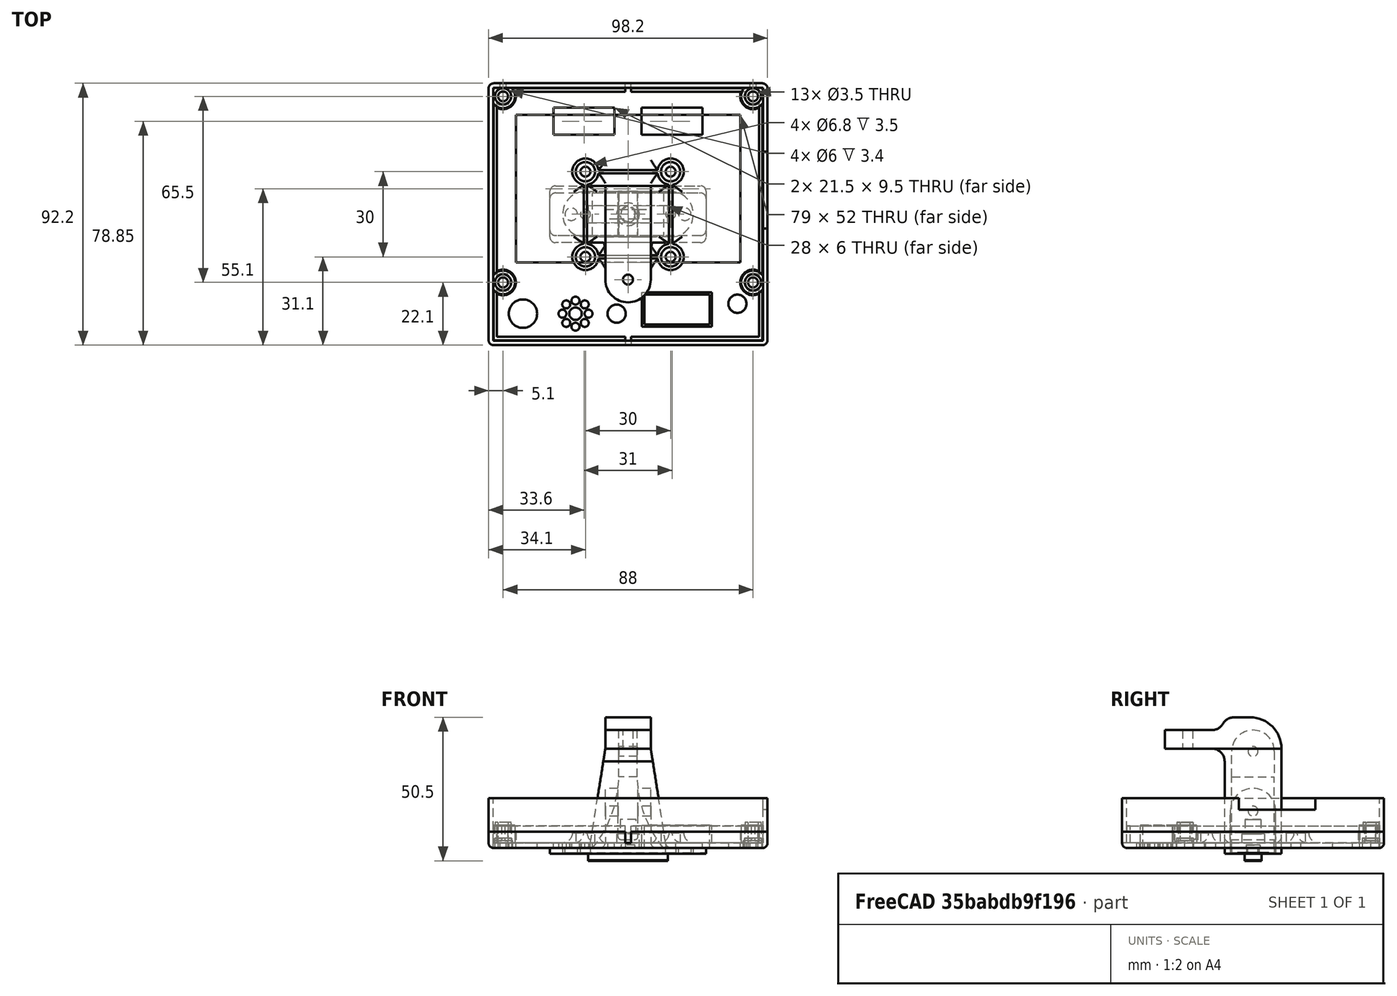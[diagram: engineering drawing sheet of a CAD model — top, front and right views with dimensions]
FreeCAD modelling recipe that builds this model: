
FCSTD DOCUMENT  (FreeCAD 0.17R13522 (Git))
Label: RRDFGSC_case
License: All rights reserved
LicenseURL: http://en.wikipedia.org/wiki/All_rights_reserved
objects: Sketcher::SketchObject×39, PartDesign::Pad×24, PartDesign::Fillet×10, PartDesign::Body×7, App::Part×7, PartDesign::Pocket×5, Spreadsheet::Sheet×2, PartDesign::AdditiveLoft×2
note: 118 computed .brp shape members not serialized (recipe doc carries the construction recipe); baked Part::Feature solids carry a one-line shape summary decoded from their .brp

FEATURE [Sketcher::SketchObject] Sketch  label="frontpanel"
  MapMode = 5
  expr: Constraints[124] = Dimensions.VMHeight
  expr: Constraints.Width = Dimensions.PCBWidth + Dimensions.PCBGap * 2 + Dimensions.WallThickness * 2
  expr: Constraints[95] = Dimensions.LCDGap
  expr: Constraints[123] = Dimensions.VMWidth
  expr: Constraints[11] = Dimensions.PCBHeight + Dimensions.PCBGap * 2 + Dimensions.WallThickness * 2
  expr: Constraints[21] = Dimensions.LCDWidth + Dimensions.LCDGap * 2
  expr: Constraints[93] = Dimensions.LCDHeight
  expr: Constraints[114] = Screws.M3HeadRadius
  expr: Constraints[112] = Dimensions.PCBHeight / 2 - Dimensions.HoleDistanceTop
  expr: Constraints[113] = Dimensions.HoleDistanceV
  expr: Constraints[94] = Dimensions.LCDGap
  expr: Constraints[108] = Dimensions.HoleDistanceH
  expr: Constraints[22] = Dimensions.LCDHeight + Dimensions.LCDGap * 2
  expr: Constraints[33] = Dimensions.PCBWidth
  expr: Constraints[96] = Dimensions.LCDWidth
  expr: Constraints[34] = Dimensions.PCBHeight
  sketch-geometry (48):
    g0: LineSegment StartX=-49.1 StartY=46.1 StartZ=0 EndX=49.1 EndY=46.1 EndZ=0
    g1: LineSegment StartX=49.1 StartY=46.1 StartZ=0 EndX=49.1 EndY=-46.1 EndZ=0
    g2: LineSegment StartX=49.1 StartY=-46.1 StartZ=0 EndX=-49.1 EndY=-46.1 EndZ=0
    g3: LineSegment StartX=-49.1 StartY=-46.1 StartZ=0 EndX=-49.1 EndY=46.1 EndZ=0
    g4: LineSegment StartX=-39.5 StartY=35 StartZ=0 EndX=39.5 EndY=35 EndZ=0
    g5: LineSegment StartX=39.5 StartY=35 StartZ=0 EndX=39.5 EndY=-17 EndZ=0
    g6: LineSegment StartX=39.5 StartY=-17 StartZ=0 EndX=-39.5 EndY=-17 EndZ=0
    g7: LineSegment StartX=-39.5 StartY=-17 StartZ=0 EndX=-39.5 EndY=35 EndZ=0
    g8: Circle CenterX=-37 CenterY=-35 CenterZ=0 NormalX=0 NormalY=0 NormalZ=1 AngleXU=0 Radius=5
    g9: LineSegment [constr] StartX=-46.5 StartY=43.5 StartZ=0 EndX=46.5 EndY=43.5 EndZ=0
    g10: LineSegment [constr] StartX=46.5 StartY=43.5 StartZ=0 EndX=46.5 EndY=-43.5 EndZ=0
    g11: LineSegment [constr] StartX=46.5 StartY=-43.5 StartZ=0 EndX=-46.5 EndY=-43.5 EndZ=0
    g12: LineSegment [constr] StartX=-46.5 StartY=-43.5 StartZ=0 EndX=-46.5 EndY=43.5 EndZ=0
    g13: Circle [constr] CenterX=-18.5 CenterY=-35 CenterZ=0 NormalX=0 NormalY=0 NormalZ=1 AngleXU=0 Radius=6
    g14: LineSegment [constr] StartX=-49.1 StartY=-35 StartZ=0 EndX=49.1 EndY=-35 EndZ=0
    g15: Circle CenterX=-4 CenterY=-35 CenterZ=0 NormalX=0 NormalY=0 NormalZ=1 AngleXU=0 Radius=3.2
    g16: Circle CenterX=-23.1 CenterY=-35 CenterZ=0 NormalX=0 NormalY=0 NormalZ=1 AngleXU=0 Radius=1.4
    g17: LineSegment [constr] StartX=-18.5 StartY=-29 StartZ=0 EndX=-18.5 EndY=-41 EndZ=0
    g18: Circle CenterX=-18.5 CenterY=-30.4 CenterZ=0 NormalX=0 NormalY=0 NormalZ=1 AngleXU=0 Radius=1.4
    g19: Circle CenterX=-13.9 CenterY=-35 CenterZ=0 NormalX=0 NormalY=0 NormalZ=1 AngleXU=0 Radius=1.4
    g20: Circle CenterX=-18.5 CenterY=-39.6 CenterZ=0 NormalX=0 NormalY=0 NormalZ=1 AngleXU=0 Radius=1.4
    g21: Circle CenterX=-18.5 CenterY=-35 CenterZ=0 NormalX=0 NormalY=0 NormalZ=1 AngleXU=0 Radius=2.2
    g22: LineSegment [constr] StartX=-22.7426 StartY=-30.7574 StartZ=0 EndX=-14.2574 EndY=-39.2426 EndZ=0
    g23: LineSegment [constr] StartX=-22.7426 StartY=-39.2426 StartZ=0 EndX=-14.2574 EndY=-30.7574 EndZ=0
    g24: Circle [constr] CenterX=-18.5 CenterY=-35 CenterZ=0 NormalX=0 NormalY=0 NormalZ=1 AngleXU=0 Radius=4.6
    g25: Circle CenterX=-21.7527 CenterY=-31.7473 CenterZ=0 NormalX=0 NormalY=0 NormalZ=1 AngleXU=0 Radius=1.4
    g26: Circle CenterX=-15.2473 CenterY=-31.7473 CenterZ=0 NormalX=0 NormalY=0 NormalZ=1 AngleXU=0 Radius=1.4
    g27: Circle CenterX=-15.2473 CenterY=-38.2527 CenterZ=0 NormalX=0 NormalY=0 NormalZ=1 AngleXU=0 Radius=1.4
    g28: Circle CenterX=-21.7527 CenterY=-38.2527 CenterZ=0 NormalX=0 NormalY=0 NormalZ=1 AngleXU=0 Radius=1.4
    g29: LineSegment [constr] StartX=-39 StartY=34.5 StartZ=0 EndX=39 EndY=34.5 EndZ=0
    g30: LineSegment [constr] StartX=39 StartY=34.5 StartZ=0 EndX=39 EndY=-16.5 EndZ=0
    g31: LineSegment [constr] StartX=39 StartY=-16.5 StartZ=0 EndX=-39 EndY=-16.5 EndZ=0
    g32: LineSegment [constr] StartX=-39 StartY=-16.5 StartZ=0 EndX=-39 EndY=34.5 EndZ=0
    g33: Circle CenterX=38.5 CenterY=-31.5 CenterZ=0 NormalX=0 NormalY=0 NormalZ=1 AngleXU=0 Radius=3.2
    g34: Circle CenterX=-44 CenterY=41.5 CenterZ=0 NormalX=0 NormalY=0 NormalZ=1 AngleXU=0 Radius=3
    g35: Circle CenterX=44 CenterY=41.5 CenterZ=0 NormalX=0 NormalY=0 NormalZ=1 AngleXU=0 Radius=3
    g36: LineSegment [constr] StartX=-44 StartY=41.5 StartZ=0 EndX=44 EndY=41.5 EndZ=0
    g37: Circle CenterX=-44 CenterY=-24 CenterZ=0 NormalX=0 NormalY=0 NormalZ=1 AngleXU=0 Radius=3
    g38: Circle CenterX=44 CenterY=-24 CenterZ=0 NormalX=0 NormalY=0 NormalZ=1 AngleXU=0 Radius=3
    g39: LineSegment [constr] StartX=-44 StartY=-24 StartZ=0 EndX=44 EndY=-24 EndZ=0
    g40: LineSegment StartX=5.75 StartY=-28.3 StartZ=0 EndX=28.75 EndY=-28.3 EndZ=0
    g41: LineSegment StartX=28.75 StartY=-28.3 StartZ=0 EndX=28.75 EndY=-38.8 EndZ=0
    g42: LineSegment StartX=28.75 StartY=-38.8 StartZ=0 EndX=5.75 EndY=-38.8 EndZ=0
    g43: LineSegment StartX=5.75 StartY=-38.8 StartZ=0 EndX=5.75 EndY=-28.3 EndZ=0
    g44: LineSegment [constr] StartX=17.25 StartY=-28.3 StartZ=0 EndX=17.25 EndY=-38.8 EndZ=0
    g45: GeomPoint X=17.25 Y=-33.25 Z=0
    g46: LineSegment [constr] StartX=28.75 StartY=-28.3 StartZ=0 EndX=38.5 EndY=-28.3 EndZ=0
    g47: LineSegment [constr] StartX=38.5 StartY=-31.5 StartZ=0 EndX=38.5 EndY=-28.3 EndZ=0
  constraints (140):
    c: Coincident(g0,g1)
    c: Coincident(g1,g2)
    c: Coincident(g2,g3)
    c: Coincident(g3,g0)
    c: Horizontal(g0)
    c: Horizontal(g2)
    c: Vertical(g1)
    c: Vertical(g3)
    c: Symmetric(g0,g0,g-2)
    c: Symmetric(g0,g2,g-1)
    c: DistanceX(g0,g0) = 98.2  'Width'
    c: DistanceY(g3,g3) = 92.2
    c: Coincident(g4,g5)
    c: Coincident(g5,g6)
    c: Coincident(g6,g7)
    c: Coincident(g7,g4)
    c: Horizontal(g4)
    c: Horizontal(g6)
    c: Vertical(g5)
    c: Vertical(g7)
    c: Symmetric(g4,g4,g-2)
    c: DistanceX(g4,g4) = 79
    c: DistanceY(g7,g7) = 52
    c: Coincident(g9,g10)
    c: Coincident(g10,g11)
    c: Coincident(g11,g12)
    c: Coincident(g12,g9)
    c: Horizontal(g9)
    c: Horizontal(g11)
    c: Vertical(g10)
    c: Vertical(g12)
    c: Symmetric(g9,g9,g-2)
    c: Symmetric(g9,g11,g-1)
    c: DistanceX(g9,g9) = 93
    c: DistanceY(g12,g12) = 87
    c: DistanceX(g11,g8) = 9.5
    c: DistanceY(g11,g8) = 8.5
    c: Radius(g8) = 5
    c: PointOnObject(g14,g3)
    c: PointOnObject(g14,g1)
    c: Horizontal(g14)
    c: PointOnObject(g8,g14)
    c: PointOnObject(g13,g14)
    c: DistanceX(g11,g13) = 28
    c: Radius(g13) = 6
    c: PointOnObject(g15,g14)
    c: Radius(g15) = 3.2
    c: PointOnObject(g16,g14)
    c: Tangent(g13,g16)
    c: Radius(g16) = 1.4
    c: PointOnObject(g17,g13)
    c: PointOnObject(g17,g13)
    c: Vertical(g17)
    c: PointOnObject(g13,g17)
    c: PointOnObject(g18,g17)
    c: Tangent(g18,g13)
    c: Equal(g16,g18)
    c: PointOnObject(g19,g14)
    c: Tangent(g19,g13)
    c: Equal(g16,g19)
    c: PointOnObject(g20,g17)
    c: Tangent(g20,g13)
    c: Equal(g16,g20)
    c: Coincident(g21,g13)
    c: PointOnObject(g22,g13)
    c: PointOnObject(g22,g13)
    c: Symmetric(g18,g16,g22)
    c: PointOnObject(g23,g13)
    c: PointOnObject(g23,g13)
    c: Symmetric(g19,g18,g23)
    c: Coincident(g24,g13)
    c: PointOnObject(g19,g24)
    c: PointOnObject(g25,g22)
    c: PointOnObject(g26,g23)
    c: PointOnObject(g27,g22)
    c: PointOnObject(g28,g24)
    c: PointOnObject(g28,g23)
    c: PointOnObject(g27,g24)
    c: PointOnObject(g26,g24)
    c: PointOnObject(g25,g24)
    c: Equal(g16,g25)
    c: Equal(g25,g26)
    c: Equal(g26,g27)
    c: Equal(g27,g28)
    c: Radius(g21) = 2.2
    c: Coincident(g29,g30)
    c: Coincident(g30,g31)
    c: Coincident(g31,g32)
    c: Coincident(g32,g29)
    c: Horizontal(g29)
    c: Horizontal(g31)
    c: Vertical(g30)
    c: Vertical(g32)
    c: DistanceY(g32,g32) = 51
    c: DistanceY(g6,g31) = 0.5
    c: DistanceX(g6,g31) = 0.5
    c: DistanceX(g29,g29) = 78
    c: DistanceY(g29,g9) = 9
    c: DistanceX(g11,g15) = 42.5
    c: DistanceX(g33,g10) = 8
    c: DistanceY(g10,g33) = 12
    c: Radius(g33) = 3.2
    c: Symmetric(g34,g35,g-2)
    c: Coincident(g36,g34)
    c: Coincident(g36,g35)
    c: Symmetric(g37,g38,g-2)
    c: Coincident(g39,g37)
    c: Coincident(g39,g38)
    c: DistanceX(g36,g36) = 88
    c: Equal(g34,g35)
    c: Equal(g35,g38)
    c: Equal(g38,g37)
    c: DistanceY(g-1,g34) = 41.5
    c: DistanceY(g37,g34) = 65.5
    c: Radius(g38) = 3
    c: Coincident(g40,g41)
    c: Coincident(g41,g42)
    c: Coincident(g42,g43)
    c: Coincident(g43,g40)
    c: Horizontal(g40)
    c: Horizontal(g42)
    c: Vertical(g41)
    c: Vertical(g43)
    c: DistanceX(g42,g42) = 23
    c: DistanceY(g43,g43) = 10.5
    c: PointOnObject(g44,g40)
    c: PointOnObject(g44,g42)
    c: Vertical(g44)
    c: Symmetric(g40,g40,g44)
    c: PointOnObject(g45,g44)
    c: Symmetric(g15,g33,g45)
    c: Coincident(g46,g40)
    c: PointOnObject(g46,g33)
    c: Horizontal(g46)
    c: Coincident(g47,g33)
    c: Coincident(g47,g46)
    c: Vertical(g47)
    c: Equal(g39,g36)
    c: DistanceY(g40,g-1) = 28.3  'VMVOffset'
    c: DistanceX(g-1,g40) = 5.75  'VMHOffset'
FEATURE [Spreadsheet::Sheet] Spreadsheet  label="Dimensions"
  cells = B4=PCBWidth; C4(PCBWidth)==93mm; B5=PCBHeight; C5(PCBHeight)==87mm; B6=PCBGap; C6(PCBGap)==1mm; B7=WallThickness; C7(WallThickness)==1.6000000000000001mm; B8=InnerWallThickness; C8(InnerWallThickness)==1.2mm; B9=InnerWallGap; C9(InnerWallGap)==0.14999999999999999mm; B10=PanelThickness; C10(PanelThickness)==1.8mm; B11=LCDWidth; C11(LCDWidth)==78mm; B12=LCDHeight; C12(LCDHeight)==51mm; B13=LCDGap; C13(LCDGap)==0.5mm; B14=VMWidth; C14(VMWidth)==23mm; B15=VMHeight; C15(VMHeight)==10.5mm; B16=HoleDistanceH; C16(HoleDistanceH)==88mm; B17=HoleDistanceV; C17(HoleDistanceV)==65.5mm; B18=HoleDistanceTop; C18(HoleDistanceTop)==2mm; B19=ArmLength; C19(ArmLength)==25mm; B20=SideArmLength; C20(SideArmLength)=35; B21=BackJoinExtraLength; C21(BackJoinExtraLength)==5mm
FEATURE [Sketcher::SketchObject] Sketch001  label="frontwalls"
  MapMode = 5
  Placement = pos=(0,0,1.8) rot=(0,0,1;0rad)
  expr: Constraints[37] = Dimensions.WallThickness
  expr: Placement.Base.z = FrontPanel.Length
  expr: Constraints[10] = Dimensions.PCBWidth + 2 * Dimensions.PCBGap + 2 * Dimensions.WallThickness
  expr: Constraints[11] = Dimensions.PCBHeight + 2 * Dimensions.PCBGap + 2 * Dimensions.WallThickness
  sketch-geometry (12):
    g0: LineSegment StartX=-49.1 StartY=46.1 StartZ=0 EndX=49.1 EndY=46.1 EndZ=0
    g1: LineSegment StartX=49.1 StartY=46.1 StartZ=0 EndX=49.1 EndY=-46.1 EndZ=0
    g2: LineSegment StartX=49.1 StartY=-46.1 StartZ=0 EndX=-49.1 EndY=-46.1 EndZ=0
    g3: LineSegment StartX=-49.1 StartY=-46.1 StartZ=0 EndX=-49.1 EndY=46.1 EndZ=0
    g4: LineSegment StartX=-47.5 StartY=44.5 StartZ=0 EndX=47.5 EndY=44.5 EndZ=0
    g5: LineSegment StartX=47.5 StartY=44.5 StartZ=0 EndX=47.5 EndY=-44.5 EndZ=0
    g6: LineSegment StartX=47.5 StartY=-44.5 StartZ=0 EndX=-47.5 EndY=-44.5 EndZ=0
    g7: LineSegment StartX=-47.5 StartY=-44.5 StartZ=0 EndX=-47.5 EndY=44.5 EndZ=0
    g8: LineSegment [constr] StartX=-47.5 StartY=-44.5 StartZ=0 EndX=-49.1 EndY=-44.5 EndZ=0
    g9: LineSegment [constr] StartX=-47.5 StartY=44.5 StartZ=0 EndX=-47.5 EndY=46.1 EndZ=0
    g10: LineSegment [constr] StartX=47.5 StartY=44.5 StartZ=0 EndX=49.1 EndY=44.5 EndZ=0
    g11: LineSegment [constr] StartX=47.5 StartY=-44.5 StartZ=0 EndX=47.5 EndY=-46.1 EndZ=0
  constraints (38):
    c: Coincident(g0,g1)
    c: Coincident(g1,g2)
    c: Coincident(g2,g3)
    c: Coincident(g3,g0)
    c: Horizontal(g0)
    c: Horizontal(g2)
    c: Vertical(g1)
    c: Vertical(g3)
    c: Symmetric(g0,g0,g-2)
    c: Symmetric(g0,g2,g-1)
    c: DistanceX(g0,g0) = 98.2
    c: DistanceY(g3,g3) = 92.2
    c: Coincident(g4,g5)
    c: Coincident(g5,g6)
    c: Coincident(g6,g7)
    c: Coincident(g7,g4)
    c: Horizontal(g4)
    c: Horizontal(g6)
    c: Vertical(g5)
    c: Vertical(g7)
    c: Symmetric(g4,g4,g-2)
    c: Symmetric(g4,g6,g-1)
    c: Coincident(g8,g6)
    c: PointOnObject(g8,g3)
    c: Horizontal(g8)
    c: Coincident(g9,g4)
    c: PointOnObject(g9,g0)
    c: Vertical(g9)
    c: Coincident(g10,g4)
    c: PointOnObject(g10,g1)
    c: Horizontal(g10)
    c: Coincident(g11,g5)
    c: PointOnObject(g11,g2)
    c: Vertical(g11)
    c: Equal(g8,g11)
    c: Equal(g11,g9)
    c: Equal(g9,g10)
    c: DistanceX(g8,g8) = 1.6
FEATURE [Sketcher::SketchObject] Sketch002  label="frontnuts1"
  MapMode = 5
  Placement = pos=(0,0,1.8) rot=(0,0,1;0rad)
  expr: Constraints[19] = Screws.M3HeadRadius
  expr: Placement.Base.z = FrontPanel.Length
  expr: Constraints[21] = Dimensions.HoleDistanceV
  expr: Constraints[20] = Dimensions.PCBHeight / 2 - Dimensions.HoleDistanceTop
  expr: Constraints[2] = Dimensions.HoleDistanceH
  sketch-geometry (10):
    g0: Circle CenterX=-44 CenterY=41.5 CenterZ=0 NormalX=0 NormalY=0 NormalZ=1 AngleXU=0 Radius=4.2
    g1: Circle CenterX=44 CenterY=41.5 CenterZ=0 NormalX=0 NormalY=0 NormalZ=1 AngleXU=0 Radius=4.2
    g2: Circle CenterX=44 CenterY=-24 CenterZ=0 NormalX=0 NormalY=0 NormalZ=1 AngleXU=0 Radius=4.2
    g3: Circle CenterX=-44 CenterY=-24 CenterZ=0 NormalX=0 NormalY=0 NormalZ=1 AngleXU=0 Radius=4.2
    g4: LineSegment [constr] StartX=-44 StartY=41.5 StartZ=0 EndX=44 EndY=41.5 EndZ=0
    g5: LineSegment [constr] StartX=-44 StartY=-24 StartZ=0 EndX=44 EndY=-24 EndZ=0
    g6: Circle CenterX=-44 CenterY=41.5 CenterZ=0 NormalX=0 NormalY=0 NormalZ=1 AngleXU=0 Radius=3
    g7: Circle CenterX=44 CenterY=41.5 CenterZ=0 NormalX=0 NormalY=0 NormalZ=1 AngleXU=0 Radius=3
    g8: Circle CenterX=44 CenterY=-24 CenterZ=0 NormalX=0 NormalY=0 NormalZ=1 AngleXU=0 Radius=3
    g9: Circle CenterX=-44 CenterY=-24 CenterZ=0 NormalX=0 NormalY=0 NormalZ=1 AngleXU=0 Radius=3
  constraints (22):
    c: Symmetric(g0,g1,g-2)
    c: Symmetric(g3,g2,g-2)
    c: DistanceX(g0,g1) = 88
    c: Coincident(g4,g0)
    c: Coincident(g4,g1)
    c: Coincident(g5,g3)
    c: Coincident(g5,g2)
    c: Equal(g4,g5)
    c: Equal(g0,g1)
    c: Equal(g1,g2)
    c: Equal(g2,g3)
    c: Radius(g0) = 4.2
    c: Coincident(g6,g0)
    c: Coincident(g7,g1)
    c: Coincident(g8,g2)
    c: Coincident(g9,g3)
    c: Equal(g6,g7)
    c: Equal(g7,g8)
    c: Equal(g8,g9)
    c: Radius(g6) = 3
    c: DistanceY(g-1,g0) = 41.5
    c: DistanceY(g3,g0) = 65.5
FEATURE [Sketcher::SketchObject] Sketch003  label="sdhole"
  MapMode = 5
  Placement = pos=(49.1,0,0) rot=(0.57735,0.57735,0.57735;2.0944rad)
  expr: Placement.Base.x = frontpanel.Constraints.Width / 2
  expr: Constraints[11] = frontwalls.Placement.Base.z + FrontWalls.Length
  expr: Constraints[8] = Dimensions.PCBHeight / 2 - 21.5mm
  sketch-geometry (4):
    g0: LineSegment StartX=22 StartY=17.5 StartZ=0 EndX=-5 EndY=17.5 EndZ=0
    g1: LineSegment StartX=-5 StartY=17.5 StartZ=0 EndX=-5 EndY=13.5 EndZ=0
    g2: LineSegment StartX=-5 StartY=13.5 StartZ=0 EndX=22 EndY=13.5 EndZ=0
    g3: LineSegment StartX=22 StartY=13.5 StartZ=0 EndX=22 EndY=17.5 EndZ=0
  constraints (12):
    c: Coincident(g0,g1)
    c: Coincident(g1,g2)
    c: Coincident(g2,g3)
    c: Coincident(g3,g0)
    c: Horizontal(g0)
    c: Horizontal(g2)
    c: Vertical(g1)
    c: Vertical(g3)
    c: DistanceX(g-1,g0) = 22
    c: DistanceX(g0,g0) = 27
    c: DistanceY(g1,g1) = 4
    c: DistanceY(g-1,g0) = 17.5
FEATURE [Sketcher::SketchObject] Sketch005  label="backwalls"
  MapMode = 5
  Placement = pos=(0,0,1.8) rot=(0,0,1;0rad)
  expr: Constraints[67] = Dimensions.WallThickness + Dimensions.InnerWallGap + Dimensions.InnerWallThickness
  expr: Constraints[7] = Dimensions.PCBHeight + 2 * Dimensions.PCBGap + 2 * Dimensions.WallThickness
  expr: Placement.Base.z = BackPanel.Length
  expr: Constraints[6] = Dimensions.PCBWidth + 2 * Dimensions.PCBGap + 2 * Dimensions.WallThickness
  sketch-geometry (24):
    g0: LineSegment StartX=49.1 StartY=46.1 StartZ=0 EndX=49.1 EndY=-46.1 EndZ=0
    g1: LineSegment StartX=-1 StartY=-46.1 StartZ=0 EndX=-49.1 EndY=-46.1 EndZ=0
    g2: LineSegment StartX=-49.1 StartY=-46.1 StartZ=0 EndX=-49.1 EndY=46.1 EndZ=0
    g3: LineSegment StartX=46.15 StartY=43.15 StartZ=0 EndX=46.15 EndY=-43.15 EndZ=0
    g4: LineSegment StartX=-1 StartY=-43.15 StartZ=0 EndX=-46.15 EndY=-43.15 EndZ=0
    g5: LineSegment StartX=-46.15 StartY=-43.15 StartZ=0 EndX=-46.15 EndY=43.15 EndZ=0
    g6: LineSegment StartX=-46.15 StartY=43.15 StartZ=0 EndX=-1 EndY=43.15 EndZ=0
    g7: LineSegment StartX=-1 StartY=43.15 StartZ=0 EndX=-1 EndY=46.1 EndZ=0
    g8: LineSegment StartX=-1 StartY=46.1 StartZ=0 EndX=-49.1 EndY=46.1 EndZ=0
    g9: LineSegment StartX=46.15 StartY=43.15 StartZ=0 EndX=1 EndY=43.15 EndZ=0
    g10: LineSegment StartX=1 StartY=43.15 StartZ=0 EndX=1 EndY=46.1 EndZ=0
    g11: LineSegment StartX=1 StartY=46.1 StartZ=0 EndX=49.1 EndY=46.1 EndZ=0
    g12: LineSegment [constr] StartX=-1 StartY=46.1 StartZ=0 EndX=1 EndY=46.1 EndZ=0
    g13: LineSegment StartX=46.15 StartY=-43.15 StartZ=0 EndX=1 EndY=-43.15 EndZ=0
    g14: LineSegment StartX=1 StartY=-43.15 StartZ=0 EndX=1 EndY=-46.1 EndZ=0
    g15: LineSegment StartX=1 StartY=-46.1 StartZ=0 EndX=49.1 EndY=-46.1 EndZ=0
    g16: LineSegment StartX=-1 StartY=-43.15 StartZ=0 EndX=-1 EndY=-46.1 EndZ=0
    g17: LineSegment [constr] StartX=-1 StartY=-43.15 StartZ=0 EndX=1 EndY=-43.15 EndZ=0
    g18: LineSegment [constr] StartX=-1 StartY=-46.1 StartZ=0 EndX=1 EndY=-46.1 EndZ=0
    g19: LineSegment [constr] StartX=-1 StartY=43.15 StartZ=0 EndX=1 EndY=43.15 EndZ=0
    g20: LineSegment [constr] StartX=-46.15 StartY=-43.15 StartZ=0 EndX=-49.1 EndY=-43.15 EndZ=0
    g21: LineSegment [constr] StartX=-46.15 StartY=43.15 StartZ=0 EndX=-46.15 EndY=46.1 EndZ=0
    g22: LineSegment [constr] StartX=46.15 StartY=43.15 StartZ=0 EndX=49.1 EndY=43.15 EndZ=0
    g23: LineSegment [constr] StartX=46.15 StartY=-43.15 StartZ=0 EndX=46.15 EndY=-46.1 EndZ=0
  constraints (68):
    c: Coincident(g1,g2)
    c: Horizontal(g1)
    c: Vertical(g0)
    c: Vertical(g2)
    c: Symmetric(g2,g0,g-2)
    c: Symmetric(g2,g1,g-1)
    c: DistanceX(g2,g0) = 98.2
    c: DistanceY(g2,g2) = 92.2
    c: Coincident(g4,g5)
    c: Horizontal(g4)
    c: Vertical(g3)
    c: Vertical(g5)
    c: Symmetric(g5,g3,g-2)
    c: Symmetric(g5,g4,g-1)
    c: Coincident(g5,g6)
    c: Horizontal(g6)
    c: Coincident(g6,g7)
    c: Vertical(g7)
    c: Coincident(g7,g8)
    c: Coincident(g8,g2)
    c: Horizontal(g8)
    c: Coincident(g3,g9)
    c: Horizontal(g9)
    c: Coincident(g9,g10)
    c: Vertical(g10)
    c: Coincident(g10,g11)
    c: Coincident(g11,g0)
    c: Horizontal(g11)
    c: Coincident(g12,g7)
    c: Coincident(g12,g10)
    c: Symmetric(g7,g10,g-2)
    c: DistanceX(g12,g12) = 2
    c: Coincident(g3,g13)
    c: Horizontal(g13)
    c: Coincident(g13,g14)
    c: Vertical(g14)
    c: Coincident(g14,g15)
    c: Coincident(g15,g0)
    c: Horizontal(g15)
    c: Coincident(g16,g4)
    c: Coincident(g16,g1)
    c: Vertical(g16)
    c: Coincident(g17,g4)
    c: Coincident(g17,g13)
    c: Coincident(g18,g1)
    c: Coincident(g18,g14)
    c: Horizontal(g18)
    c: Symmetric(g4,g13,g-2)
    c: Equal(g18,g17)
    c: Equal(g17,g12)
    c: Coincident(g19,g6)
    c: Coincident(g19,g9)
    c: Coincident(g20,g4)
    c: PointOnObject(g20,g2)
    c: Horizontal(g20)
    c: Coincident(g21,g5)
    c: PointOnObject(g21,g8)
    c: Vertical(g21)
    c: Coincident(g22,g3)
    c: PointOnObject(g22,g0)
    c: Horizontal(g22)
    c: Coincident(g23,g3)
    c: PointOnObject(g23,g15)
    c: Vertical(g23)
    c: Equal(g20,g21)
    c: Equal(g21,g22)
    c: Equal(g22,g23)
    c: DistanceX(g20,g20) = 2.95
FEATURE [Sketcher::SketchObject] Sketch006  label="backnuts3"
  MapMode = 5
  Placement = pos=(0,0,5.8) rot=(0,0,1;0rad)
  expr: Constraints[11] = Screws.M3Radius + 1.1000000000000001mm
  expr: Constraints[21] = Dimensions.HoleDistanceV
  expr: Constraints[20] = Dimensions.PCBHeight / 2 - Dimensions.HoleDistanceTop
  expr: Constraints[19] = Screws.M3Radius
  expr: Placement.Base.z = BackPanel.Length + BackNuts2.Length
  expr: Constraints[2] = Dimensions.HoleDistanceH
  sketch-geometry (10):
    g0: Circle CenterX=-44 CenterY=41.5 CenterZ=0 NormalX=0 NormalY=0 NormalZ=1 AngleXU=0 Radius=2.85
    g1: Circle CenterX=44 CenterY=41.5 CenterZ=0 NormalX=0 NormalY=0 NormalZ=1 AngleXU=0 Radius=2.85
    g2: Circle CenterX=44 CenterY=-24 CenterZ=0 NormalX=0 NormalY=0 NormalZ=1 AngleXU=0 Radius=2.85
    g3: Circle CenterX=-44 CenterY=-24 CenterZ=0 NormalX=0 NormalY=0 NormalZ=1 AngleXU=0 Radius=2.85
    g4: LineSegment [constr] StartX=-44 StartY=41.5 StartZ=0 EndX=44 EndY=41.5 EndZ=0
    g5: LineSegment [constr] StartX=-44 StartY=-24 StartZ=0 EndX=44 EndY=-24 EndZ=0
    g6: Circle CenterX=-44 CenterY=41.5 CenterZ=0 NormalX=0 NormalY=0 NormalZ=1 AngleXU=0 Radius=1.75
    g7: Circle CenterX=44 CenterY=41.5 CenterZ=0 NormalX=0 NormalY=0 NormalZ=1 AngleXU=0 Radius=1.75
    g8: Circle CenterX=44 CenterY=-24 CenterZ=0 NormalX=0 NormalY=0 NormalZ=1 AngleXU=0 Radius=1.75
    g9: Circle CenterX=-44 CenterY=-24 CenterZ=0 NormalX=0 NormalY=0 NormalZ=1 AngleXU=0 Radius=1.75
  constraints (22):
    c: Symmetric(g0,g1,g-2)
    c: Symmetric(g3,g2,g-2)
    c: DistanceX(g0,g1) = 88
    c: Coincident(g4,g0)
    c: Coincident(g4,g1)
    c: Coincident(g5,g3)
    c: Coincident(g5,g2)
    c: Equal(g4,g5)
    c: Equal(g0,g1)
    c: Equal(g1,g2)
    c: Equal(g2,g3)
    c: Radius(g0) = 2.85
    c: Coincident(g6,g0)
    c: Coincident(g7,g1)
    c: Coincident(g8,g2)
    c: Coincident(g9,g3)
    c: Equal(g6,g7)
    c: Equal(g7,g8)
    c: Equal(g8,g9)
    c: Radius(g6) = 1.75
    c: DistanceY(g-1,g0) = 41.5
    c: DistanceY(g3,g0) = 65.5
FEATURE [Sketcher::SketchObject] Sketch007  label="backpanel"
  MapMode = 5
  expr: Constraints[9] = Dimensions.PCBHeight + Dimensions.PCBGap * 2 + Dimensions.WallThickness * 2
  expr: Constraints[29] = Dimensions.LCDWidth
  expr: Constraints[18] = Dimensions.PCBWidth
  expr: Constraints[19] = Dimensions.PCBHeight
  expr: Constraints[28] = Dimensions.LCDHeight
  expr: Constraints[8] = Dimensions.PCBWidth + Dimensions.PCBGap * 2 + Dimensions.WallThickness * 2
  sketch-geometry (26):
    g0: LineSegment StartX=-49.1 StartY=46.1 StartZ=0 EndX=49.1 EndY=46.1 EndZ=0
    g1: LineSegment StartX=49.1 StartY=46.1 StartZ=0 EndX=49.1 EndY=-46.1 EndZ=0
    g2: LineSegment StartX=49.1 StartY=-46.1 StartZ=0 EndX=-49.1 EndY=-46.1 EndZ=0
    g3: LineSegment StartX=-49.1 StartY=-46.1 StartZ=0 EndX=-49.1 EndY=46.1 EndZ=0
    g4: LineSegment [constr] StartX=-46.5 StartY=43.5 StartZ=0 EndX=46.5 EndY=43.5 EndZ=0
    g5: LineSegment [constr] StartX=46.5 StartY=43.5 StartZ=0 EndX=46.5 EndY=-43.5 EndZ=0
    g6: LineSegment [constr] StartX=46.5 StartY=-43.5 StartZ=0 EndX=-46.5 EndY=-43.5 EndZ=0
    g7: LineSegment [constr] StartX=-46.5 StartY=-43.5 StartZ=0 EndX=-46.5 EndY=43.5 EndZ=0
    g8: LineSegment [constr] StartX=-39 StartY=34.5 StartZ=0 EndX=39 EndY=34.5 EndZ=0
    g9: LineSegment [constr] StartX=39 StartY=34.5 StartZ=0 EndX=39 EndY=-16.5 EndZ=0
    g10: LineSegment [constr] StartX=39 StartY=-16.5 StartZ=0 EndX=-39 EndY=-16.5 EndZ=0
    g11: LineSegment [constr] StartX=-39 StartY=-16.5 StartZ=0 EndX=-39 EndY=34.5 EndZ=0
    g12: LineSegment StartX=4.75 StartY=37.5 StartZ=0 EndX=26.25 EndY=37.5 EndZ=0
    g13: LineSegment StartX=26.25 StartY=37.5 StartZ=0 EndX=26.25 EndY=28 EndZ=0
    g14: LineSegment StartX=26.25 StartY=28 StartZ=0 EndX=4.75 EndY=28 EndZ=0
    g15: LineSegment StartX=4.75 StartY=28 StartZ=0 EndX=4.75 EndY=37.5 EndZ=0
    g16: LineSegment StartX=-26.25 StartY=37.5 StartZ=0 EndX=-4.75 EndY=37.5 EndZ=0
    g17: LineSegment StartX=-4.75 StartY=37.5 StartZ=0 EndX=-4.75 EndY=28 EndZ=0
    g18: LineSegment StartX=-4.75 StartY=28 StartZ=0 EndX=-26.25 EndY=28 EndZ=0
    g19: LineSegment StartX=-26.25 StartY=28 StartZ=0 EndX=-26.25 EndY=37.5 EndZ=0
    g20: Circle CenterX=-15 CenterY=-15 CenterZ=0 NormalX=0 NormalY=0 NormalZ=1 AngleXU=0 Radius=1.75
    g21: Circle CenterX=15 CenterY=-15 CenterZ=0 NormalX=0 NormalY=0 NormalZ=1 AngleXU=0 Radius=1.75
    g22: Circle CenterX=-15 CenterY=15 CenterZ=0 NormalX=0 NormalY=0 NormalZ=1 AngleXU=0 Radius=1.75
    g23: Circle CenterX=15 CenterY=15 CenterZ=0 NormalX=0 NormalY=0 NormalZ=1 AngleXU=0 Radius=1.75
    g24: LineSegment [constr] StartX=-15 StartY=-15 StartZ=0 EndX=15 EndY=-15 EndZ=0
    g25: LineSegment [constr] StartX=15 StartY=-15 StartZ=0 EndX=15 EndY=15 EndZ=0
  constraints (76):
    c: Coincident(g0,g1)
    c: Coincident(g1,g2)
    c: Coincident(g2,g3)
    c: Coincident(g3,g0)
    c: Horizontal(g0)
    c: Horizontal(g2)
    c: Vertical(g1)
    c: Vertical(g3)
    c: DistanceX(g0,g0) = 98.2
    c: DistanceY(g3,g3) = 92.2
    c: Coincident(g4,g5)
    c: Coincident(g5,g6)
    c: Coincident(g6,g7)
    c: Coincident(g7,g4)
    c: Horizontal(g4)
    c: Horizontal(g6)
    c: Vertical(g5)
    c: Vertical(g7)
    c: DistanceX(g4,g4) = 93
    c: DistanceY(g7,g7) = 87
    c: Coincident(g8,g9)
    c: Coincident(g9,g10)
    c: Coincident(g10,g11)
    c: Coincident(g11,g8)
    c: Horizontal(g8)
    c: Horizontal(g10)
    c: Vertical(g9)
    c: Vertical(g11)
    c: DistanceY(g11,g11) = 51
    c: DistanceX(g8,g8) = 78
    c: DistanceY(g8,g4) = 9
    c: Symmetric(g6,g5,g-2)
    c: Symmetric(g0,g0,g-2)
    c: Symmetric(g0,g2,g-1)
    c: Symmetric(g4,g4,g-2)
    c: Symmetric(g4,g6,g-1)
    c: Symmetric(g8,g8,g-2)
    c: Coincident(g12,g13)
    c: Coincident(g13,g14)
    c: Coincident(g14,g15)
    c: Coincident(g15,g12)
    c: Horizontal(g12)
    c: Horizontal(g14)
    c: Vertical(g13)
    c: Vertical(g15)
    c: DistanceX(g12,g12) = 21.5
    c: DistanceY(g15,g15) = 9.5
    c: DistanceY(g12,g4) = 6
    c: Coincident(g16,g17)
    c: Coincident(g17,g18)
    c: Coincident(g18,g19)
    c: Coincident(g19,g16)
    c: Horizontal(g16)
    c: Horizontal(g18)
    c: Vertical(g17)
    c: Vertical(g19)
    c: Equal(g16,g12)
    c: Equal(g17,g15)
    c: Symmetric(g16,g12,g-2)
    c: DistanceX(g17,g14) = 9.5
    c: Symmetric(g20,g21,g-2)
    c: Equal(g20,g21)
    c: Radius(g20) = 1.75
    c: DistanceX(g20,g21) = 30  'AttacherHoleDistance'
    c: Equal(g-1,g23)
    c: Equal(g23,g22)
    c: Equal(g22,g21)
    c: Symmetric(g21,g23,g-1)
    c: Symmetric(g20,g22,g-1)
    c: Coincident(g24,g20)
    c: Horizontal(g24)
    c: Coincident(g25,g21)
    c: Vertical(g25)
    c: Equal(g25,g24)
    c: Coincident(g25,g23)
    c: Coincident(g24,g21)
FEATURE [Sketcher::SketchObject] Sketch009  label="backnuts2"
  MapMode = 5
  Placement = pos=(0,0,1.8) rot=(0,0,1;0rad)
  expr: Placement.Base.z = BackPanel.Length
  expr: Constraints[2] = Dimensions.HoleDistanceH
  expr: Constraints[21] = Dimensions.HoleDistanceV
  expr: Constraints[20] = Dimensions.PCBHeight / 2 - Dimensions.HoleDistanceTop
  sketch-geometry (10):
    g0: Circle CenterX=-44 CenterY=41.5 CenterZ=0 NormalX=0 NormalY=0 NormalZ=1 AngleXU=0 Radius=4.5
    g1: Circle CenterX=44 CenterY=41.5 CenterZ=0 NormalX=0 NormalY=0 NormalZ=1 AngleXU=0 Radius=4.5
    g2: Circle CenterX=44 CenterY=-24 CenterZ=0 NormalX=0 NormalY=0 NormalZ=1 AngleXU=0 Radius=4.5
    g3: Circle CenterX=-44 CenterY=-24 CenterZ=0 NormalX=0 NormalY=0 NormalZ=1 AngleXU=0 Radius=4.5
    g4: LineSegment [constr] StartX=-44 StartY=41.5 StartZ=0 EndX=44 EndY=41.5 EndZ=0
    g5: LineSegment [constr] StartX=-44 StartY=-24 StartZ=0 EndX=44 EndY=-24 EndZ=0
    g6: Circle CenterX=-44 CenterY=41.5 CenterZ=0 NormalX=0 NormalY=0 NormalZ=1 AngleXU=0 Radius=1.75
    g7: Circle CenterX=44 CenterY=41.5 CenterZ=0 NormalX=0 NormalY=0 NormalZ=1 AngleXU=0 Radius=1.75
    g8: Circle CenterX=44 CenterY=-24 CenterZ=0 NormalX=0 NormalY=0 NormalZ=1 AngleXU=0 Radius=1.75
    g9: Circle CenterX=-44 CenterY=-24 CenterZ=0 NormalX=0 NormalY=0 NormalZ=1 AngleXU=0 Radius=1.75
  constraints (22):
    c: Symmetric(g0,g1,g-2)
    c: Symmetric(g3,g2,g-2)
    c: DistanceX(g0,g1) = 88
    c: Coincident(g4,g0)
    c: Coincident(g4,g1)
    c: Coincident(g5,g3)
    c: Coincident(g5,g2)
    c: Equal(g4,g5)
    c: Equal(g0,g1)
    c: Equal(g1,g2)
    c: Equal(g2,g3)
    c: Radius(g0) = 4.5
    c: Coincident(g6,g0)
    c: Coincident(g7,g1)
    c: Coincident(g8,g2)
    c: Coincident(g9,g3)
    c: Equal(g6,g7)
    c: Equal(g7,g8)
    c: Equal(g8,g9)
    c: Radius(g6) = 1.75
    c: DistanceY(g-1,g0) = 41.5
    c: DistanceY(g3,g0) = 65.5
FEATURE [Sketcher::SketchObject] Sketch010  label="armadapter_backjoin"
  MapMode = 5
  expr: Constraints.Width = armadapter_hingebase.Constraints.Radius * 2
  expr: Constraints[12] = Sketch007.Constraints.AttacherHoleDistance
  sketch-geometry (8):
    g0: Circle CenterX=-15 CenterY=0 CenterZ=0 NormalX=0 NormalY=0 NormalZ=1 AngleXU=0 Radius=1.75
    g1: Circle CenterX=15 CenterY=0 CenterZ=0 NormalX=0 NormalY=0 NormalZ=1 AngleXU=0 Radius=1.75
    g2: LineSegment StartX=-15 StartY=8 StartZ=0 EndX=15 EndY=8 EndZ=0
    g3: LineSegment [constr] StartX=15 StartY=8 StartZ=0 EndX=15 EndY=-8 EndZ=0
    g4: LineSegment StartX=15 StartY=-8 StartZ=0 EndX=-15 EndY=-8 EndZ=0
    g5: LineSegment [constr] StartX=-15 StartY=-8 StartZ=0 EndX=-15 EndY=8 EndZ=0
    g6: ArcOfCircle CenterX=-15 CenterY=0 CenterZ=0 NormalX=0 NormalY=0 NormalZ=1 AngleXU=0 Radius=8 StartAngle=1.5708 EndAngle=4.71239
    g7: ArcOfCircle CenterX=15 CenterY=0 CenterZ=0 NormalX=0 NormalY=0 NormalZ=1 AngleXU=0 Radius=8 StartAngle=4.71239 EndAngle=7.85398
  constraints (22):
    c: PointOnObject(g0,g-1)
    c: PointOnObject(g1,g-1)
    c: Equal(g0,g1)
    c: Radius(g0) = 1.75
    c: Coincident(g2,g3)
    c: Coincident(g3,g4)
    c: Coincident(g4,g5)
    c: Coincident(g5,g2)
    c: Horizontal(g4)
    c: Vertical(g3)
    c: Vertical(g5)
    c: Symmetric(g2,g2,g-2)
    c: DistanceX(g2,g2) = 30
    c: PointOnObject(g0,g5)
    c: PointOnObject(g1,g3)
    c: DistanceY(g5,g5) = 16  'Width'
    c: Coincident(g6,g0)
    c: Coincident(g6,g2)
    c: Coincident(g6,g4)
    c: Coincident(g7,g1)
    c: Coincident(g7,g2)
    c: Coincident(g7,g3)
FEATURE [Sketcher::SketchObject] Sketch011  label="armadapter_hingebase"
  MapMode = 5
  Placement = pos=(0,0,0) rot=(0.57735,0.57735,0.57735;2.0944rad)
  expr: Constraints.VerticalOffset = Constraints.Radius + Dimensions.BackJoinExtraLength
  expr: Constraints[15] = Screws.M3Radius
  sketch-geometry (6):
    g0: LineSegment StartX=-8 StartY=0 StartZ=0 EndX=8 EndY=0 EndZ=0
    g1: LineSegment StartX=8 StartY=0 StartZ=0 EndX=8 EndY=13 EndZ=0
    g2: LineSegment [constr] StartX=8 StartY=13 StartZ=0 EndX=-8 EndY=13 EndZ=0
    g3: LineSegment StartX=-8 StartY=13 StartZ=0 EndX=-8 EndY=0 EndZ=0
    g4: ArcOfCircle CenterX=0 CenterY=13 CenterZ=0 NormalX=0 NormalY=0 NormalZ=1 AngleXU=0 Radius=8 StartAngle=0 EndAngle=3.14159
    g5: Circle CenterX=0 CenterY=13 CenterZ=0 NormalX=0 NormalY=0 NormalZ=1 AngleXU=0 Radius=1.75
  constraints (17):
    c: Coincident(g0,g1)
    c: Coincident(g1,g2)
    c: Coincident(g2,g3)
    c: Coincident(g3,g0)
    c: Horizontal(g0)
    c: Horizontal(g2)
    c: Vertical(g1)
    c: Vertical(g3)
    c: PointOnObject(g0,g-1)
    c: Symmetric(g0,g0,g-2)
    c: PointOnObject(g4,g2)
    c: Coincident(g4,g2)
    c: Coincident(g4,g1)
    c: DistanceY(g3,g3) = 13  'VerticalOffset'
    c: Coincident(g5,g4)
    c: Radius(g5) = 1.75
    c: Radius(g4) = 8  'Radius'
FEATURE [Sketcher::SketchObject] Sketch012  label="armadapter_hingecavity"
  MapMode = 5
  Placement = pos=(0,0,3) rot=(0.707107,0.707107,0;3.14159rad)
  expr: Placement.Base.z = armadapter_hingebase.Constraints.VerticalOffset - armadapter_hingebase.Constraints.Radius - 2mm
  expr: Constraints[10] = armadapter_backjoin.Constraints.Width
  sketch-geometry (4):
    g0: LineSegment StartX=-8 StartY=3.5 StartZ=0 EndX=8 EndY=3.5 EndZ=0
    g1: LineSegment StartX=8 StartY=3.5 StartZ=0 EndX=8 EndY=-3.5 EndZ=0
    g2: LineSegment StartX=8 StartY=-3.5 StartZ=0 EndX=-8 EndY=-3.5 EndZ=0
    g3: LineSegment StartX=-8 StartY=-3.5 StartZ=0 EndX=-8 EndY=3.5 EndZ=0
  constraints (12):
    c: Coincident(g0,g1)
    c: Coincident(g1,g2)
    c: Coincident(g2,g3)
    c: Coincident(g3,g0)
    c: Horizontal(g0)
    c: Horizontal(g2)
    c: Vertical(g1)
    c: Vertical(g3)
    c: Symmetric(g0,g2,g-1)
    c: DistanceY(g2,g0) = 7  'Width'
    c: DistanceX(g0,g0) = 16
    c: Symmetric(g0,g0,g-2)
FEATURE [Sketcher::SketchObject] Sketch014  label="arm_2020_base"
  MapMode = 5
  sketch-geometry (10):
    g0: LineSegment StartX=-25.5 StartY=7.5 StartZ=0 EndX=25.5 EndY=7.5 EndZ=0
    g1: LineSegment StartX=27.5 StartY=5.5 StartZ=0 EndX=27.5 EndY=-5.5 EndZ=0
    g2: LineSegment StartX=25.5 StartY=-7.5 StartZ=0 EndX=-25.5 EndY=-7.5 EndZ=0
    g3: LineSegment StartX=-27.5 StartY=-5.5 StartZ=0 EndX=-27.5 EndY=5.5 EndZ=0
    g4: ArcOfCircle CenterX=25.5 CenterY=-5.5 CenterZ=0 NormalX=0 NormalY=0 NormalZ=1 AngleXU=0 Radius=2 StartAngle=4.71239 EndAngle=6.28319
    g5: ArcOfCircle CenterX=-25.5 CenterY=-5.5 CenterZ=0 NormalX=0 NormalY=0 NormalZ=1 AngleXU=0 Radius=2 StartAngle=3.14159 EndAngle=4.71239
    g6: ArcOfCircle CenterX=-25.5 CenterY=5.5 CenterZ=0 NormalX=0 NormalY=0 NormalZ=1 AngleXU=0 Radius=2 StartAngle=1.5708 EndAngle=3.14159
    g7: ArcOfCircle CenterX=25.5 CenterY=5.5 CenterZ=0 NormalX=0 NormalY=0 NormalZ=1 AngleXU=0 Radius=2 StartAngle=0 EndAngle=1.5708
    g8: Circle CenterX=-20 CenterY=0 CenterZ=0 NormalX=0 NormalY=0 NormalZ=1 AngleXU=0 Radius=2.2
    g9: Circle CenterX=20 CenterY=0 CenterZ=0 NormalX=0 NormalY=0 NormalZ=1 AngleXU=0 Radius=2.2
  constraints (25):
    c: Horizontal(g2)
    c: Vertical(g1)
    c: Vertical(g3)
    c: Tangent(g1,g4) = 1.5708
    c: Tangent(g2,g4) = 1.5708
    c: Tangent(g2,g5) = 1.5708
    c: Tangent(g3,g5) = 1.5708
    c: Tangent(g0,g6) = 1.5708
    c: Tangent(g3,g6) = 1.5708
    c: Tangent(g0,g7) = 1.5708
    c: Tangent(g1,g7) = 1.5708
    c: Radius(g6) = 2
    c: Equal(g7,g6)
    c: Equal(g6,g5)
    c: Equal(g5,g4)
    c: Symmetric(g2,g0,g-1)
    c: Symmetric(g0,g0,g-2)
    c: DistanceX(g3,g1) = 55
    c: DistanceY(g2,g0) = 15
    c: PointOnObject(g8,g-1)
    c: PointOnObject(g9,g-1)
    c: Equal(g8,g9)
    c: Symmetric(g8,g9,g-2)
    c: DistanceX(g8,g9) = 40  'ScrewDistance'
    c: Radius(g8) = 2.2
FEATURE [Sketcher::SketchObject] Sketch015  label="arm_2020_base_groove"
  MapMode = 5
  Placement = pos=(0,0,-1.8) rot=(1,0,0;3.14159rad)
  expr: Placement.Base.z = -Arm2020Base.Length
  expr: Constraints[10] = arm_2020_base.Constraints.ScrewDistance - 12mm
  sketch-geometry (4):
    g0: LineSegment StartX=-14 StartY=3 StartZ=0 EndX=14 EndY=3 EndZ=0
    g1: LineSegment StartX=14 StartY=3 StartZ=0 EndX=14 EndY=-3 EndZ=0
    g2: LineSegment StartX=14 StartY=-3 StartZ=0 EndX=-14 EndY=-3 EndZ=0
    g3: LineSegment StartX=-14 StartY=-3 StartZ=0 EndX=-14 EndY=3 EndZ=0
  constraints (12):
    c: Coincident(g0,g1)
    c: Coincident(g1,g2)
    c: Coincident(g2,g3)
    c: Coincident(g3,g0)
    c: Horizontal(g0)
    c: Horizontal(g2)
    c: Vertical(g1)
    c: Vertical(g3)
    c: Symmetric(g0,g2,g-1)
    c: Symmetric(g0,g0,g-2)
    c: DistanceX(g0,g0) = 28
    c: DistanceY(g3,g3) = 6
FEATURE [Sketcher::SketchObject] Sketch016  label="arm_2020_start_L"
  MapMode = 5
  sketch-geometry (4):
    g0: LineSegment StartX=-12.5 StartY=7.5 StartZ=0 EndX=12.5 EndY=7.5 EndZ=0
    g1: LineSegment StartX=12.5 StartY=7.5 StartZ=0 EndX=12.5 EndY=-7.5 EndZ=0
    g2: LineSegment StartX=12.5 StartY=-7.5 StartZ=0 EndX=-12.5 EndY=-7.5 EndZ=0
    g3: LineSegment StartX=-12.5 StartY=-7.5 StartZ=0 EndX=-12.5 EndY=7.5 EndZ=0
  constraints (13):
    c: Horizontal(g0)
    c: Horizontal(g2)
    c: Vertical(g1)
    c: Symmetric(g0,g2,g-1)
    c: Symmetric(g3,g1,g-2)
    c: DistanceX(g3,g1) = 25
    c: Coincident(g0,g1)
    c: Coincident(g0,g3)
    c: Coincident(g2,g3)
    c: Coincident(g1,g2)
    c: Equal(g0,g2)
    c: Equal(g3,g1)
    c: DistanceY(g3,g3) = 15  'Width'
FEATURE [Sketcher::SketchObject] Sketch017  label="arm_2020_start_H"
  MapMode = 5
  Placement = pos=(0,0,25) rot=(0,0,1;0rad)
  expr: Constraints.Width = armadapter_hingecavity.Constraints.Width - 0.5mm
  expr: Placement.Base.z = Dimensions.ArmLength
  sketch-geometry (4):
    g0: LineSegment StartX=-3.25 StartY=7.5 StartZ=0 EndX=3.25 EndY=7.5 EndZ=0
    g1: LineSegment StartX=3.25 StartY=7.5 StartZ=0 EndX=3.25 EndY=-7.5 EndZ=0
    g2: LineSegment StartX=3.25 StartY=-7.5 StartZ=0 EndX=-3.25 EndY=-7.5 EndZ=0
    g3: LineSegment StartX=-3.25 StartY=-7.5 StartZ=0 EndX=-3.25 EndY=7.5 EndZ=0
  constraints (12):
    c: Coincident(g0,g1)
    c: Coincident(g1,g2)
    c: Coincident(g2,g3)
    c: Coincident(g3,g0)
    c: Horizontal(g0)
    c: Horizontal(g2)
    c: Vertical(g1)
    c: Vertical(g3)
    c: Symmetric(g0,g2,g-1)
    c: Symmetric(g0,g0,g-2)
    c: DistanceX(g0,g0) = 6.5  'Width'
    c: DistanceY(g3,g3) = 15
FEATURE [Sketcher::SketchObject] Sketch018  label="arm_2020_hinge"
  MapMode = 5
  Placement = pos=(0,0,25) rot=(0.57735,0.57735,0.57735;2.0944rad)
  expr: Placement.Base.z = Dimensions.ArmLength
  sketch-geometry (6):
    g0: LineSegment StartX=7.5 StartY=0 StartZ=0 EndX=-7.5 EndY=0 EndZ=0
    g1: LineSegment StartX=-7.5 StartY=0 StartZ=0 EndX=-7.5 EndY=9 EndZ=0
    g2: LineSegment StartX=7.5 StartY=9 StartZ=0 EndX=7.5 EndY=0 EndZ=0
    g3: ArcOfCircle CenterX=0 CenterY=9 CenterZ=0 NormalX=0 NormalY=0 NormalZ=1 AngleXU=0 Radius=7.5 StartAngle=0 EndAngle=3.14159
    g4: LineSegment [constr] StartX=-7.5 StartY=9 StartZ=0 EndX=7.5 EndY=9 EndZ=0
    g5: Circle CenterX=0 CenterY=9 CenterZ=0 NormalX=0 NormalY=0 NormalZ=1 AngleXU=0 Radius=1.75
  constraints (17):
    c: Coincident(g0,g1)
    c: Coincident(g2,g0)
    c: Vertical(g1)
    c: Vertical(g2)
    c: PointOnObject(g0,g-1)
    c: Symmetric(g0,g0,g-2)
    c: DistanceX(g0,g0) = 15
    c: DistanceY(g1,g1) = 9
    c: PointOnObject(g3,g-2)
    c: Coincident(g3,g1)
    c: Coincident(g3,g2)
    c: Equal(g2,g1)
    c: Coincident(g4,g1)
    c: Coincident(g4,g2)
    c: PointOnObject(g3,g4)
    c: Coincident(g5,g3)
    c: Radius(g5) = 1.75
FEATURE [Sketcher::SketchObject] Sketch020  label="resetbutton_base"
  MapMode = 5
  sketch-geometry (1):
    g0: Circle CenterX=0 CenterY=0 CenterZ=0 NormalX=0 NormalY=0 NormalZ=1 AngleXU=0 Radius=4
  constraints (2):
    c: Coincident(g0,g-1)
    c: Radius(g0) = 4
FEATURE [Sketcher::SketchObject] Sketch021  label="resetbutton_button"
  MapMode = 5
  Placement = pos=(0,0,5) rot=(0,0,1;0rad)
  expr: Placement.Base.z = ResetButtonBase.Length
  sketch-geometry (1):
    g0: Circle CenterX=0 CenterY=0 CenterZ=0 NormalX=0 NormalY=0 NormalZ=1 AngleXU=0 Radius=2.8
  constraints (2):
    c: Coincident(g0,g-1)
    c: Radius(g0) = 2.8
FEATURE [Sketcher::SketchObject] Sketch022  label="resetbutton_hole"
  MapMode = 5
  Placement = pos=(0,0,0) rot=(1,0,0;3.14159rad)
  sketch-geometry (1):
    g0: Circle CenterX=0 CenterY=0 CenterZ=0 NormalX=0 NormalY=0 NormalZ=1 AngleXU=0 Radius=2.5
  constraints (2):
    c: Coincident(g0,g-1)
    c: Radius(g0) = 2.5
FEATURE [PartDesign::Pad] Pad  label="FrontPanel"
  Length = 1.8
  Length2 = 100
  Profile = -> Sketch
  Type = 0
  expr: Length = Dimensions.PanelThickness
FEATURE [PartDesign::Pad] Pad001  label="FrontWalls"
  BaseFeature = -> Pad
  Length = 15.7
  Length2 = 100
  Profile = -> Sketch001
  Type = 0
  expr: Length = 17.5mm - Dimensions.PanelThickness
FEATURE [PartDesign::Pad] Pad002  label="FrontNuts1"
  BaseFeature = -> Pad001
  Length = 1.6
  Length2 = 100
  Profile = -> Sketch002
  Type = 0
  expr: Length = Screws.M3HeadHeight - frontnuts1.Placement.Base.z
FEATURE [PartDesign::Pad] Pad003  label="BackPanel"
  Length = 1.8
  Length2 = 100
  Profile = -> Sketch007
  Type = 0
  expr: Length = Dimensions.PanelThickness
FEATURE [PartDesign::Pad] Pad004  label="BackWalls"
  BaseFeature = -> Pad003
  Length = 4
  Length2 = 100
  Profile = -> Sketch005
  Type = 0
FEATURE [PartDesign::Pad] Pad008  label="ArmAdapterHingebase"
  Length = 16
  Length2 = 100
  Midplane = true
  Placement = pos=(0,0,0) rot=(0.57735,0.57735,0.57735;2.0944rad)
  Profile = -> Sketch011
  Type = 0
  expr: Length = armadapter_hingebase.Constraints.Radius * 2
FEATURE [PartDesign::Pad] Pad009  label="ArmAdapterBackJoin"
  BaseFeature = -> Pad008
  Length = 1.8
  Length2 = 100
  Placement = pos=(0,0,0) rot=(0.57735,0.57735,0.57735;2.0944rad)
  Profile = -> Sketch010
  Reversed = true
  Type = 0
  expr: Length = Dimensions.PanelThickness
FEATURE [PartDesign::Pocket] Pocket002  label="ArmAdapterHingeCavity"
  BaseFeature = -> Pad009
  Length = 0
  Length2 = 0
  Placement = pos=(0,0,0) rot=(0.57735,0.57735,0.57735;2.0944rad)
  Profile = -> Sketch012
  Refine = true
  Type = 2
FEATURE [PartDesign::Fillet] Fillet001
  Base = -> Pocket002 [Edge43,Edge39]
  BaseFeature = -> Pocket002
  Placement = pos=(0,0,0) rot=(0.57735,0.57735,0.57735;2.0944rad)
  Radius = 1
FEATURE [PartDesign::Pad] Pad010  label="Arm2020Base"
  Length = 1.8
  Length2 = 100
  Profile = -> Sketch014
  Reversed = true
  Type = 0
  expr: Length = Dimensions.PanelThickness
FEATURE [Sketcher::SketchObject] Sketch025  label="arm_2020_start_M"
  MapMode = 5
  Placement = pos=(0,0,5) rot=(0,0,1;0rad)
  sketch-geometry (4):
    g0: LineSegment StartX=-9 StartY=7.5 StartZ=0 EndX=9 EndY=7.5 EndZ=0
    g1: LineSegment StartX=9 StartY=7.5 StartZ=0 EndX=9 EndY=-7.5 EndZ=0
    g2: LineSegment StartX=9 StartY=-7.5 StartZ=0 EndX=-9 EndY=-7.5 EndZ=0
    g3: LineSegment StartX=-9 StartY=-7.5 StartZ=0 EndX=-9 EndY=7.5 EndZ=0
  constraints (13):
    c: Horizontal(g0)
    c: Horizontal(g2)
    c: Vertical(g1)
    c: Symmetric(g0,g2,g-1)
    c: Symmetric(g3,g1,g-2)
    c: DistanceX(g3,g1) = 18
    c: Coincident(g0,g1)
    c: Coincident(g0,g3)
    c: Coincident(g2,g3)
    c: Coincident(g1,g2)
    c: Equal(g0,g2)
    c: Equal(g3,g1)
    c: DistanceY(g3,g3) = 15  'Width'
FEATURE [PartDesign::AdditiveLoft] AdditiveLoft
  BaseFeature = -> Pad010
  Closed = false
  Profile = -> Sketch016
  Ruled = false
  Sections = -> [Sketch025,Sketch017]
FEATURE [PartDesign::Pad] Pad011  label="Arm2020Hinge"
  BaseFeature = -> AdditiveLoft
  Length = 6.5
  Length2 = 100
  Midplane = true
  Profile = -> Sketch018
  Refine = true
  Type = 0
  expr: Length = arm_2020_start_H.Constraints.Width
FEATURE [PartDesign::Pad] Pad012  label="Arm2020BaseGroove"
  BaseFeature = -> Pad011
  Length = 2.5
  Length2 = 100
  Profile = -> Sketch015
  Type = 0
FEATURE [PartDesign::Body] Body003  label="ArmBody"
  Group = -> [Sketch014,Sketch016,Sketch017,Sketch018,Sketch015,Pad010,AdditiveLoft,Pad011,Sketch025,Pad012]
  Origin = -> Origin004
  Tip = -> Pad012
FEATURE [App::Part] Part  label="Arm"
  Group = -> [Body003]
  License = CC BY 3.0
  LicenseURL = http://creativecommons.org/licenses/by/3.0/
  Origin = -> Origin002
FEATURE [Spreadsheet::Sheet] Spreadsheet001  label="Screws"
  cells = B2=M3Radius; C2(M3Radius)==1.75mm; B3=M3HeadRadius; C3(M3HeadRadius)==3mm; B4=M3HeadHeight; C4(M3HeadHeight)==3.3999999999999999mm; B5=M3NutRadius; C5(M3NutRadius)==3.3999999999999999mm; B6=M3NutHeight; C6(M3NutHeight)==2.6000000000000001mm; B7=M3NutDuctWidth; C7(M3NutDuctWidth)==6mm; B8=M4Radius; C8(M4Radius)==2.2000000000000002mm; B9=M4HeadRadius; C9(M4HeadRadius)==3.7000000000000002mm; B10=M4HeadHeight; C10(M4HeadHeight)==4mm; B11=M4NutRadius; C11(M4NutRadius)==4.2000000000000002mm; B12=M4NutHeight; C12(M4NutHeight)==3.2999999999999998mm; B13=M5Radius; C13(M5Radius)==2.6600000000000001mm; B14=M5HeadRadius; C14(M5HeadRadius)==4.5mm; B15=M5HeadHeight; C15(M5HeadHeight)==5mm; B16=M5NutRadius; C16(M5NutRadius)==4.75mm; B17=M5NutHeight; C17(M5NutHeight)==4mm
FEATURE [Sketcher::SketchObject] Sketch026  label="frontnuts2"
  MapMode = 5
  Placement = pos=(0,0,3.4) rot=(0,0,1;0rad)
  expr: Constraints[19] = Screws.M3Radius
  expr: Placement.Base.z = frontnuts1.Placement.Base.z + FrontNuts1.Length
  expr: Constraints[21] = Dimensions.HoleDistanceV
  expr: Constraints[20] = Dimensions.PCBHeight / 2 - Dimensions.HoleDistanceTop
  expr: Constraints[2] = Dimensions.HoleDistanceH
  sketch-geometry (10):
    g0: Circle CenterX=-44 CenterY=41.5 CenterZ=0 NormalX=0 NormalY=0 NormalZ=1 AngleXU=0 Radius=4.2
    g1: Circle CenterX=44 CenterY=41.5 CenterZ=0 NormalX=0 NormalY=0 NormalZ=1 AngleXU=0 Radius=4.2
    g2: Circle CenterX=44 CenterY=-24 CenterZ=0 NormalX=0 NormalY=0 NormalZ=1 AngleXU=0 Radius=4.2
    g3: Circle CenterX=-44 CenterY=-24 CenterZ=0 NormalX=0 NormalY=0 NormalZ=1 AngleXU=0 Radius=4.2
    g4: LineSegment [constr] StartX=-44 StartY=41.5 StartZ=0 EndX=44 EndY=41.5 EndZ=0
    g5: LineSegment [constr] StartX=-44 StartY=-24 StartZ=0 EndX=44 EndY=-24 EndZ=0
    g6: Circle CenterX=-44 CenterY=41.5 CenterZ=0 NormalX=0 NormalY=0 NormalZ=1 AngleXU=0 Radius=1.75
    g7: Circle CenterX=44 CenterY=41.5 CenterZ=0 NormalX=0 NormalY=0 NormalZ=1 AngleXU=0 Radius=1.75
    g8: Circle CenterX=44 CenterY=-24 CenterZ=0 NormalX=0 NormalY=0 NormalZ=1 AngleXU=0 Radius=1.75
    g9: Circle CenterX=-44 CenterY=-24 CenterZ=0 NormalX=0 NormalY=0 NormalZ=1 AngleXU=0 Radius=1.75
  constraints (22):
    c: Symmetric(g0,g1,g-2)
    c: Symmetric(g3,g2,g-2)
    c: DistanceX(g0,g1) = 88
    c: Coincident(g4,g0)
    c: Coincident(g4,g1)
    c: Coincident(g5,g3)
    c: Coincident(g5,g2)
    c: Equal(g4,g5)
    c: Equal(g0,g1)
    c: Equal(g1,g2)
    c: Equal(g2,g3)
    c: Radius(g0) = 4.2
    c: Coincident(g6,g0)
    c: Coincident(g7,g1)
    c: Coincident(g8,g2)
    c: Coincident(g9,g3)
    c: Equal(g6,g7)
    c: Equal(g7,g8)
    c: Equal(g8,g9)
    c: Radius(g6) = 1.75
    c: DistanceY(g-1,g0) = 41.5
    c: DistanceY(g3,g0) = 65.5
FEATURE [PartDesign::Pad] Pad013  label="FrontNuts2"
  BaseFeature = -> Pad002
  Length = 4.6
  Length2 = 100
  Profile = -> Sketch026
  Type = 0
  expr: Length = 8mm - (frontnuts1.Placement.Base.z + FrontNuts1.Length)
FEATURE [Sketcher::SketchObject] Sketch027  label="vmframe"
  AttachmentOffset = pos=(0,0,1.8) rot=(0,0,1;0rad)
  MapMode = 5
  Placement = pos=(0,0,1.8) rot=(0,0,1;0rad)
  Support = -> [XY_Plane]
  expr: Constraints[11] = frontpanel.Constraints.VMHOffset
  expr: Constraints[10] = Sketch.Constraints.VMVOffset
  expr: Constraints[9] = Dimensions.VMHeight
  expr: Constraints[8] = Dimensions.VMWidth
  expr: AttachmentOffset.Base.z = Dimensions.PanelThickness
  sketch-geometry (12):
    g0: LineSegment StartX=5.75 StartY=-28.3 StartZ=0 EndX=28.75 EndY=-28.3 EndZ=0
    g1: LineSegment StartX=28.75 StartY=-28.3 StartZ=0 EndX=28.75 EndY=-38.8 EndZ=0
    g2: LineSegment StartX=28.75 StartY=-38.8 StartZ=0 EndX=5.75 EndY=-38.8 EndZ=0
    g3: LineSegment StartX=5.75 StartY=-38.8 StartZ=0 EndX=5.75 EndY=-28.3 EndZ=0
    g4: LineSegment StartX=4.93 StartY=-27.48 StartZ=0 EndX=29.57 EndY=-27.48 EndZ=0
    g5: LineSegment StartX=29.57 StartY=-27.48 StartZ=0 EndX=29.57 EndY=-39.62 EndZ=0
    g6: LineSegment StartX=29.57 StartY=-39.62 StartZ=0 EndX=4.93 EndY=-39.62 EndZ=0
    g7: LineSegment StartX=4.93 StartY=-39.62 StartZ=0 EndX=4.93 EndY=-27.48 EndZ=0
    g8: LineSegment [constr] StartX=28.75 StartY=-38.8 StartZ=0 EndX=28.75 EndY=-39.62 EndZ=0
    g9: LineSegment [constr] StartX=28.75 StartY=-28.3 StartZ=0 EndX=29.57 EndY=-28.3 EndZ=0
    g10: LineSegment [constr] StartX=5.75 StartY=-28.3 StartZ=0 EndX=5.75 EndY=-27.48 EndZ=0
    g11: LineSegment [constr] StartX=5.75 StartY=-38.8 StartZ=0 EndX=4.93 EndY=-38.8 EndZ=0
  constraints (36):
    c: Coincident(g0,g1)
    c: Coincident(g1,g2)
    c: Coincident(g2,g3)
    c: Coincident(g3,g0)
    c: Horizontal(g0)
    c: Horizontal(g2)
    c: Vertical(g1)
    c: Vertical(g3)
    c: DistanceX(g2,g2) = 23
    c: DistanceY(g3,g3) = 10.5
    c: DistanceY(g0,g-1) = 28.3
    c: DistanceX(g-1,g0) = 5.75
    c: Coincident(g4,g5)
    c: Coincident(g5,g6)
    c: Coincident(g6,g7)
    c: Coincident(g7,g4)
    c: Horizontal(g4)
    c: Horizontal(g6)
    c: Vertical(g5)
    c: Vertical(g7)
    c: DistanceX(g1,g5) = 0.82
    c: Coincident(g8,g1)
    c: PointOnObject(g8,g6)
    c: Vertical(g8)
    c: Coincident(g9,g0)
    c: PointOnObject(g9,g5)
    c: Horizontal(g9)
    c: Coincident(g10,g0)
    c: PointOnObject(g10,g4)
    c: Vertical(g10)
    c: Coincident(g11,g2)
    c: PointOnObject(g11,g7)
    c: Horizontal(g11)
    c: Equal(g8,g9)
    c: Equal(g9,g10)
    c: Equal(g10,g11)
FEATURE [PartDesign::Pad] Pad014  label="VmFrame"
  BaseFeature = -> Pad013
  Length = 6.2
  Length2 = 100
  Profile = -> Sketch027
  Type = 0
  expr: Length = frontnuts2.Placement.Base.z + FrontNuts2.Length - FrontPanel.Length
FEATURE [PartDesign::Pocket] Pocket  label="SDHole"
  BaseFeature = -> Pad014
  Length = 1.6
  Length2 = 100
  Profile = -> Sketch003
  Refine = true
  Type = 0
  expr: Length = Dimensions.WallThickness
FEATURE [PartDesign::Fillet] Fillet
  Base = -> Pocket [Edge165,Edge21,Edge22,Edge163,Edge166,Edge20,Edge19,Edge164]
  BaseFeature = -> Pocket
  Radius = 1.799
  expr: Radius = Spreadsheet.PanelThickness - 0.001mm
FEATURE [PartDesign::Body] Body  label="FrontBody"
  Group = -> [Sketch,Sketch001,Sketch002,Sketch003,Pad,Pad001,Pad002,Pad013,Pad014,Pocket,Sketch026,Sketch027,Fillet]
  Origin = -> Origin
  Tip = -> Fillet
FEATURE [App::Part] Part002  label="Front"
  Group = -> [Body]
  License = CC BY 3.0
  LicenseURL = http://creativecommons.org/licenses/by/3.0/
  Origin = -> Origin006
FEATURE [Sketcher::SketchObject] Sketch028  label="armadapter2_backjoin"
  MapMode = 5
  expr: Constraints.Width = armadapter2_hingebase.Constraints.Radius * 2
  expr: Constraints[12] = Sketch007.Constraints.AttacherHoleDistance
  sketch-geometry (8):
    g0: Circle CenterX=-15 CenterY=0 CenterZ=0 NormalX=0 NormalY=0 NormalZ=1 AngleXU=0 Radius=1.75
    g1: Circle CenterX=15 CenterY=0 CenterZ=0 NormalX=0 NormalY=0 NormalZ=1 AngleXU=0 Radius=1.75
    g2: LineSegment StartX=-15 StartY=8 StartZ=0 EndX=15 EndY=8 EndZ=0
    g3: LineSegment [constr] StartX=15 StartY=8 StartZ=0 EndX=15 EndY=-8 EndZ=0
    g4: LineSegment StartX=15 StartY=-8 StartZ=0 EndX=-15 EndY=-8 EndZ=0
    g5: LineSegment [constr] StartX=-15 StartY=-8 StartZ=0 EndX=-15 EndY=8 EndZ=0
    g6: ArcOfCircle CenterX=-15 CenterY=0 CenterZ=0 NormalX=0 NormalY=0 NormalZ=1 AngleXU=0 Radius=8 StartAngle=1.5708 EndAngle=4.71239
    g7: ArcOfCircle CenterX=15 CenterY=0 CenterZ=0 NormalX=0 NormalY=0 NormalZ=1 AngleXU=0 Radius=8 StartAngle=4.71239 EndAngle=7.85398
  constraints (22):
    c: PointOnObject(g0,g-1)
    c: PointOnObject(g1,g-1)
    c: Equal(g0,g1)
    c: Radius(g0) = 1.75
    c: Coincident(g2,g3)
    c: Coincident(g3,g4)
    c: Coincident(g4,g5)
    c: Coincident(g5,g2)
    c: Horizontal(g4)
    c: Vertical(g3)
    c: Vertical(g5)
    c: Symmetric(g2,g2,g-2)
    c: DistanceX(g2,g2) = 30
    c: PointOnObject(g0,g5)
    c: PointOnObject(g1,g3)
    c: DistanceY(g5,g5) = 16  'Width'
    c: Coincident(g6,g0)
    c: Coincident(g6,g2)
    c: Coincident(g6,g4)
    c: Coincident(g7,g1)
    c: Coincident(g7,g2)
    c: Coincident(g7,g3)
FEATURE [Sketcher::SketchObject] Sketch029  label="armadapter2_hingebase"
  MapMode = 5
  Placement = pos=(0,0,0) rot=(0,0.707107,0.707107;3.14159rad)
  expr: Constraints.VerticalOffset = Constraints.Radius + Dimensions.BackJoinExtraLength
  expr: Constraints[15] = Screws.M3Radius
  sketch-geometry (6):
    g0: LineSegment StartX=-8 StartY=0 StartZ=0 EndX=8 EndY=0 EndZ=0
    g1: LineSegment StartX=8 StartY=0 StartZ=0 EndX=8 EndY=13 EndZ=0
    g2: LineSegment [constr] StartX=8 StartY=13 StartZ=0 EndX=-8 EndY=13 EndZ=0
    g3: LineSegment StartX=-8 StartY=13 StartZ=0 EndX=-8 EndY=0 EndZ=0
    g4: ArcOfCircle CenterX=0 CenterY=13 CenterZ=0 NormalX=0 NormalY=0 NormalZ=1 AngleXU=0 Radius=8 StartAngle=0 EndAngle=3.14159
    g5: Circle CenterX=0 CenterY=13 CenterZ=0 NormalX=0 NormalY=0 NormalZ=1 AngleXU=0 Radius=1.75
  constraints (17):
    c: Coincident(g0,g1)
    c: Coincident(g1,g2)
    c: Coincident(g2,g3)
    c: Coincident(g3,g0)
    c: Horizontal(g0)
    c: Horizontal(g2)
    c: Vertical(g1)
    c: Vertical(g3)
    c: PointOnObject(g0,g-1)
    c: Symmetric(g0,g0,g-2)
    c: PointOnObject(g4,g2)
    c: Coincident(g4,g2)
    c: Coincident(g4,g1)
    c: DistanceY(g3,g3) = 13  'VerticalOffset'
    c: Coincident(g5,g4)
    c: Radius(g5) = 1.75
    c: Radius(g4) = 8  'Radius'
FEATURE [PartDesign::Pad] Pad015  label="ArmAdapter2Hingebase"
  Length = 16
  Length2 = 100
  Midplane = true
  Placement = pos=(0,0,0) rot=(0,0.707107,0.707107;3.14159rad)
  Profile = -> Sketch029
  Type = 0
  expr: Length = armadapter2_hingebase.Constraints.Radius * 2
FEATURE [Sketcher::SketchObject] Sketch030  label="armadapter2_hingecavity"
  MapMode = 5
  Placement = pos=(0,0,3) rot=(0,1,0;3.14159rad)
  expr: Placement.Base.z = armadapter2_hingebase.Constraints.VerticalOffset - armadapter2_hingebase.Constraints.Radius - 2mm
  expr: Constraints[10] = armadapter2_backjoin.Constraints.Width
  sketch-geometry (4):
    g0: LineSegment StartX=-8 StartY=3.5 StartZ=0 EndX=8 EndY=3.5 EndZ=0
    g1: LineSegment StartX=8 StartY=3.5 StartZ=0 EndX=8 EndY=-3.5 EndZ=0
    g2: LineSegment StartX=8 StartY=-3.5 StartZ=0 EndX=-8 EndY=-3.5 EndZ=0
    g3: LineSegment StartX=-8 StartY=-3.5 StartZ=0 EndX=-8 EndY=3.5 EndZ=0
  constraints (12):
    c: Coincident(g0,g1)
    c: Coincident(g1,g2)
    c: Coincident(g2,g3)
    c: Coincident(g3,g0)
    c: Horizontal(g0)
    c: Horizontal(g2)
    c: Vertical(g1)
    c: Vertical(g3)
    c: Symmetric(g0,g2,g-1)
    c: DistanceY(g2,g0) = 7  'Width'
    c: DistanceX(g0,g0) = 16
    c: Symmetric(g0,g0,g-2)
FEATURE [PartDesign::Pad] Pad016  label="ArmAdapter2BackJoin"
  BaseFeature = -> Pad015
  Length = 1.8
  Length2 = 100
  Placement = pos=(0,0,0) rot=(0,0.707107,0.707107;3.14159rad)
  Profile = -> Sketch028
  Reversed = true
  Type = 0
  expr: Length = Dimensions.PanelThickness
FEATURE [PartDesign::Pocket] Pocket003  label="ArmAdapter2HingeCavity"
  BaseFeature = -> Pad016
  Length = 0
  Length2 = 0
  Placement = pos=(0,0,0) rot=(0,0.707107,0.707107;3.14159rad)
  Profile = -> Sketch030
  Type = 2
FEATURE [PartDesign::Fillet] Fillet003
  Base = -> Pocket003 [Edge14,Edge20,Edge49,Edge47]
  BaseFeature = -> Pocket003
  Placement = pos=(0,0,0) rot=(0,0.707107,0.707107;3.14159rad)
  Radius = 1
FEATURE [PartDesign::Body] Body005  label="Adapter2Body"
  Group = -> [Pad015,Pad016,Pocket003,Sketch028,Sketch030,Sketch029,Fillet003]
  Origin = -> Origin003
  Tip = -> Fillet003
FEATURE [App::Part] Part005  label="Adapter2"
  Group = -> [Body005]
  License = CC BY 3.0
  LicenseURL = http://creativecommons.org/licenses/by/3.0/
  Origin = -> Origin009
  Placement = pos=(-15,0,25) rot=(0,0,1;1.5708rad)
FEATURE [PartDesign::Pad] Pad017  label="ResetButtonBase"
  Length = 5
  Length2 = 100
  Profile = -> Sketch020
  Type = 0
FEATURE [PartDesign::Pad] Pad018
  BaseFeature = -> Pad017
  Length = 5
  Length2 = 100
  Profile = -> Sketch021
  Type = 0
FEATURE [PartDesign::Pocket] Pocket004
  BaseFeature = -> Pad018
  Length = 1
  Length2 = 100
  Profile = -> Sketch022
  Type = 0
FEATURE [PartDesign::Body] Body004  label="ResetBody"
  Group = -> [Sketch020,Sketch021,Sketch022,Pad017,Pad018,Pocket004]
  Origin = -> Origin008
  Tip = -> Pocket004
FEATURE [App::Part] Part003  label="ResetButton"
  Group = -> [Body004]
  License = CC BY 3.0
  LicenseURL = http://creativecommons.org/licenses/by/3.0/
  Origin = -> Origin007
  Placement = pos=(-4,-34.9,7) rot=(0,1,0;3.14159rad)
FEATURE [Sketcher::SketchObject] Sketch031  label="backpanel001"
  MapMode = 5
  expr: Constraints[153] = Dimensions.HoleDistanceH
  expr: Constraints[20] = Dimensions.PCBHeight
  expr: Constraints[161] = Dimensions.PCBHeight / 2 - Dimensions.HoleDistanceTop
  expr: Constraints[160] = Dimensions.HoleDistanceV
  expr: Constraints[19] = Dimensions.PCBWidth
  expr: Constraints[152] = Screws.M3NutRadius
  expr: Constraints[29] = Dimensions.LCDHeight
  expr: Constraints[10] = Dimensions.PCBHeight + Dimensions.PCBGap * 2 + Dimensions.WallThickness * 2
  expr: Constraints[9] = Dimensions.PCBWidth + Dimensions.PCBGap * 2 + Dimensions.WallThickness * 2
  expr: Constraints[30] = Dimensions.LCDWidth
  sketch-geometry (56):
    g0: LineSegment [constr] StartX=-44 StartY=41.5 StartZ=0 EndX=44 EndY=41.5 EndZ=0
    g1: LineSegment [constr] StartX=-44 StartY=-24 StartZ=0 EndX=44 EndY=-24 EndZ=0
    g2: LineSegment StartX=-49.1 StartY=46.1 StartZ=0 EndX=49.1 EndY=46.1 EndZ=0
    g3: LineSegment StartX=49.1 StartY=46.1 StartZ=0 EndX=49.1 EndY=-46.1 EndZ=0
    g4: LineSegment StartX=49.1 StartY=-46.1 StartZ=0 EndX=-49.1 EndY=-46.1 EndZ=0
    g5: LineSegment StartX=-49.1 StartY=-46.1 StartZ=0 EndX=-49.1 EndY=46.1 EndZ=0
    g6: LineSegment [constr] StartX=-46.5 StartY=43.5 StartZ=0 EndX=46.5 EndY=43.5 EndZ=0
    g7: LineSegment [constr] StartX=46.5 StartY=43.5 StartZ=0 EndX=46.5 EndY=-43.5 EndZ=0
    g8: LineSegment [constr] StartX=46.5 StartY=-43.5 StartZ=0 EndX=-46.5 EndY=-43.5 EndZ=0
    g9: LineSegment [constr] StartX=-46.5 StartY=-43.5 StartZ=0 EndX=-46.5 EndY=43.5 EndZ=0
    g10: LineSegment [constr] StartX=-39 StartY=34.5 StartZ=0 EndX=39 EndY=34.5 EndZ=0
    g11: LineSegment [constr] StartX=39 StartY=34.5 StartZ=0 EndX=39 EndY=-16.5 EndZ=0
    g12: LineSegment [constr] StartX=39 StartY=-16.5 StartZ=0 EndX=-39 EndY=-16.5 EndZ=0
    g13: LineSegment [constr] StartX=-39 StartY=-16.5 StartZ=0 EndX=-39 EndY=34.5 EndZ=0
    g14: LineSegment StartX=4.75 StartY=37.5 StartZ=0 EndX=26.25 EndY=37.5 EndZ=0
    g15: LineSegment StartX=26.25 StartY=37.5 StartZ=0 EndX=26.25 EndY=28 EndZ=0
    g16: LineSegment StartX=26.25 StartY=28 StartZ=0 EndX=4.75 EndY=28 EndZ=0
    g17: LineSegment StartX=4.75 StartY=28 StartZ=0 EndX=4.75 EndY=37.5 EndZ=0
    g18: LineSegment StartX=-26.25 StartY=37.5 StartZ=0 EndX=-4.75 EndY=37.5 EndZ=0
    g19: LineSegment StartX=-4.75 StartY=37.5 StartZ=0 EndX=-4.75 EndY=28 EndZ=0
    g20: LineSegment StartX=-4.75 StartY=28 StartZ=0 EndX=-26.25 EndY=28 EndZ=0
    g21: LineSegment StartX=-26.25 StartY=28 StartZ=0 EndX=-26.25 EndY=37.5 EndZ=0
    g22: Circle CenterX=-15 CenterY=-15 CenterZ=0 NormalX=0 NormalY=0 NormalZ=1 AngleXU=0 Radius=1.75
    g23: Circle CenterX=15 CenterY=-15 CenterZ=0 NormalX=0 NormalY=0 NormalZ=1 AngleXU=0 Radius=1.75
    g24: Circle CenterX=-15 CenterY=15 CenterZ=0 NormalX=0 NormalY=0 NormalZ=1 AngleXU=0 Radius=1.75
    g25: Circle CenterX=15 CenterY=15 CenterZ=0 NormalX=0 NormalY=0 NormalZ=1 AngleXU=0 Radius=1.75
    g26: LineSegment [constr] StartX=-15 StartY=-15 StartZ=0 EndX=15 EndY=-15 EndZ=0
    g27: LineSegment [constr] StartX=15 StartY=-15 StartZ=0 EndX=15 EndY=15 EndZ=0
    g28: LineSegment StartX=-42.3 StartY=38.5555 StartZ=0 EndX=-40.6 EndY=41.5 EndZ=0
    g29: LineSegment StartX=-40.6 StartY=41.5 StartZ=0 EndX=-42.3 EndY=44.4445 EndZ=0
    g30: LineSegment StartX=-42.3 StartY=44.4445 StartZ=0 EndX=-45.7 EndY=44.4445 EndZ=0
    g31: LineSegment StartX=-45.7 StartY=44.4445 StartZ=0 EndX=-47.4 EndY=41.5 EndZ=0
    g32: LineSegment StartX=-47.4 StartY=41.5 StartZ=0 EndX=-45.7 EndY=38.5555 EndZ=0
    g33: LineSegment StartX=-45.7 StartY=38.5555 StartZ=0 EndX=-42.3 EndY=38.5555 EndZ=0
    g34: Circle [constr] CenterX=-44 CenterY=41.5 CenterZ=0 NormalX=0 NormalY=0 NormalZ=1 AngleXU=0 Radius=3.4
    g35: LineSegment StartX=45.7 StartY=38.5555 StartZ=0 EndX=47.4 EndY=41.5 EndZ=0
    g36: LineSegment StartX=47.4 StartY=41.5 StartZ=0 EndX=45.7 EndY=44.4445 EndZ=0
    g37: LineSegment StartX=45.7 StartY=44.4445 StartZ=0 EndX=42.3 EndY=44.4445 EndZ=0
    g38: LineSegment StartX=42.3 StartY=44.4445 StartZ=0 EndX=40.6 EndY=41.5 EndZ=0
    g39: LineSegment StartX=40.6 StartY=41.5 StartZ=0 EndX=42.3 EndY=38.5555 EndZ=0
    g40: LineSegment StartX=42.3 StartY=38.5555 StartZ=0 EndX=45.7 EndY=38.5555 EndZ=0
    g41: Circle [constr] CenterX=44 CenterY=41.5 CenterZ=0 NormalX=0 NormalY=0 NormalZ=1 AngleXU=0 Radius=3.4
    g42: LineSegment StartX=45.7 StartY=-26.9445 StartZ=0 EndX=47.4 EndY=-24 EndZ=0
    g43: LineSegment StartX=47.4 StartY=-24 StartZ=0 EndX=45.7 EndY=-21.0555 EndZ=0
    g44: LineSegment StartX=45.7 StartY=-21.0555 StartZ=0 EndX=42.3 EndY=-21.0555 EndZ=0
    g45: LineSegment StartX=42.3 StartY=-21.0555 StartZ=0 EndX=40.6 EndY=-24 EndZ=0
    g46: LineSegment StartX=40.6 StartY=-24 StartZ=0 EndX=42.3 EndY=-26.9445 EndZ=0
    g47: LineSegment StartX=42.3 StartY=-26.9445 StartZ=0 EndX=45.7 EndY=-26.9445 EndZ=0
    g48: Circle [constr] CenterX=44 CenterY=-24 CenterZ=0 NormalX=0 NormalY=0 NormalZ=1 AngleXU=0 Radius=3.4
    g49: LineSegment StartX=-42.3 StartY=-26.9445 StartZ=0 EndX=-40.6 EndY=-24 EndZ=0
    g50: LineSegment StartX=-40.6 StartY=-24 StartZ=0 EndX=-42.3 EndY=-21.0555 EndZ=0
    g51: LineSegment StartX=-42.3 StartY=-21.0555 StartZ=0 EndX=-45.7 EndY=-21.0555 EndZ=0
    g52: LineSegment StartX=-45.7 StartY=-21.0555 StartZ=0 EndX=-47.4 EndY=-24 EndZ=0
    g53: LineSegment StartX=-47.4 StartY=-24 StartZ=0 EndX=-45.7 EndY=-26.9445 EndZ=0
    g54: LineSegment StartX=-45.7 StartY=-26.9445 StartZ=0 EndX=-42.3 EndY=-26.9445 EndZ=0
    g55: Circle [constr] CenterX=-44 CenterY=-24 CenterZ=0 NormalX=0 NormalY=0 NormalZ=1 AngleXU=0 Radius=3.4
  constraints (146):
    c: Equal(g0,g1)
    c: Coincident(g2,g3)
    c: Coincident(g3,g4)
    c: Coincident(g4,g5)
    c: Coincident(g5,g2)
    c: Horizontal(g2)
    c: Horizontal(g4)
    c: Vertical(g3)
    c: Vertical(g5)
    c: DistanceX(g2,g2) = 98.2
    c: DistanceY(g5,g5) = 92.2
    c: Coincident(g6,g7)
    c: Coincident(g7,g8)
    c: Coincident(g8,g9)
    c: Coincident(g9,g6)
    c: Horizontal(g6)
    c: Horizontal(g8)
    c: Vertical(g7)
    c: Vertical(g9)
    c: DistanceX(g6,g6) = 93
    c: DistanceY(g9,g9) = 87
    c: Coincident(g10,g11)
    c: Coincident(g11,g12)
    c: Coincident(g12,g13)
    c: Coincident(g13,g10)
    c: Horizontal(g10)
    c: Horizontal(g12)
    c: Vertical(g11)
    c: Vertical(g13)
    c: DistanceY(g13,g13) = 51
    c: DistanceX(g10,g10) = 78
    c: DistanceY(g10,g6) = 9
    c: Symmetric(g8,g7,g-2)
    c: Symmetric(g2,g2,g-2)
    c: Symmetric(g2,g4,g-1)
    c: Symmetric(g6,g6,g-2)
    c: Symmetric(g6,g8,g-1)
    c: Symmetric(g10,g10,g-2)
    c: Coincident(g14,g15)
    c: Coincident(g15,g16)
    c: Coincident(g16,g17)
    c: Coincident(g17,g14)
    c: Horizontal(g14)
    c: Horizontal(g16)
    c: Vertical(g15)
    c: Vertical(g17)
    c: DistanceX(g14,g14) = 21.5
    c: DistanceY(g17,g17) = 9.5
    c: DistanceY(g14,g6) = 6
    c: Coincident(g18,g19)
    c: Coincident(g19,g20)
    c: Coincident(g20,g21)
    c: Coincident(g21,g18)
    c: Horizontal(g18)
    c: Horizontal(g20)
    c: Vertical(g19)
    c: Vertical(g21)
    c: Equal(g18,g14)
    c: Equal(g19,g17)
    c: Symmetric(g18,g14,g-2)
    c: DistanceX(g19,g16) = 9.5
    c: Symmetric(g22,g23,g-2)
    c: Equal(g22,g23)
    c: Radius(g22) = 1.75
    c: DistanceX(g22,g23) = 30  'AttacherHoleDistance'
    c: Equal(g-1,g25)
    c: Equal(g25,g24)
    c: Equal(g24,g23)
    c: Symmetric(g23,g25,g-1)
    c: Symmetric(g22,g24,g-1)
    c: Coincident(g26,g22)
    c: Horizontal(g26)
    c: Coincident(g27,g23)
    c: Vertical(g27)
    c: Equal(g27,g26)
    c: Coincident(g27,g25)
    c: Coincident(g26,g23)
    c: Coincident(g28,g29)
    c: Coincident(g29,g30)
    c: Coincident(g30,g31)
    c: Coincident(g31,g32)
    c: Coincident(g32,g33)
    c: Coincident(g33,g28)
    c: Equal(g28, g29-g33) x5
    c: PointOnObject(g28,g34)
    c: PointOnObject(g29,g34)
    c: PointOnObject(g30,g34)
    c: PointOnObject(g31,g34)
    c: PointOnObject(g32,g34)
    c: PointOnObject(g33,g34)
    c: Coincident(g35,g36)
    c: Coincident(g36,g37)
    c: Coincident(g37,g38)
    c: Coincident(g38,g39)
    c: Coincident(g39,g40)
    c: Coincident(g40,g35)
    c: Equal(g35, g36-g40) x5
    c: PointOnObject(g35,g41)
    c: PointOnObject(g36,g41)
    c: PointOnObject(g37,g41)
    c: PointOnObject(g38,g41)
    c: PointOnObject(g39,g41)
    c: PointOnObject(g40,g41)
    c: Coincident(g42,g43)
    c: Coincident(g43,g44)
    c: Coincident(g44,g45)
    c: Coincident(g45,g46)
    c: Coincident(g46,g47)
    c: Coincident(g47,g42)
    c: Equal(g42, g43-g47) x5
    c: PointOnObject(g42,g48)
    c: PointOnObject(g43,g48)
    c: PointOnObject(g44,g48)
    c: PointOnObject(g45,g48)
    c: PointOnObject(g46,g48)
    c: PointOnObject(g47,g48)
    c: Coincident(g49,g50)
    c: Coincident(g50,g51)
    c: Coincident(g51,g52)
    c: Coincident(g52,g53)
    c: Coincident(g53,g54)
    c: Coincident(g54,g49)
    c: Equal(g49, g50-g54) x5
    c: PointOnObject(g49,g55)
    c: PointOnObject(g50,g55)
    c: PointOnObject(g51,g55)
    c: PointOnObject(g52,g55)
    c: PointOnObject(g53,g55)
    c: PointOnObject(g54,g55)
    c: Horizontal(g30)
    c: Horizontal(g37)
    c: Horizontal(g44)
    c: Horizontal(g51)
    c: Equal(g55,g48)
    c: Equal(g48,g41)
    c: Equal(g41,g34)
    c: Radius(g48) = 3.4
    c: DistanceX(g0,g0) = 88
    c: Symmetric(g0,g0,g-2)
    c: Coincident(g41,g0)
    c: Coincident(g34,g0)
    c: Symmetric(g1,g1,g-2)
    c: Coincident(g55,g1)
    c: Coincident(g1,g48)
    c: DistanceY(g1,g0) = 65.5
    c: DistanceY(g-1,g0) = 41.5
FEATURE [Sketcher::SketchObject] Sketch032  label="armadapter_backjoin001"
  MapMode = 5
  expr: Constraints.Width = armadapter_hingebase.Constraints.Radius * 2
  expr: Constraints[12] = Sketch007.Constraints.AttacherHoleDistance
  sketch-geometry (8):
    g0: Circle CenterX=-15 CenterY=0 CenterZ=0 NormalX=0 NormalY=0 NormalZ=1 AngleXU=0 Radius=1.75
    g1: Circle CenterX=15 CenterY=0 CenterZ=0 NormalX=0 NormalY=0 NormalZ=1 AngleXU=0 Radius=1.75
    g2: LineSegment StartX=-15 StartY=8 StartZ=0 EndX=15 EndY=8 EndZ=0
    g3: LineSegment [constr] StartX=15 StartY=8 StartZ=0 EndX=15 EndY=-8 EndZ=0
    g4: LineSegment StartX=15 StartY=-8 StartZ=0 EndX=-15 EndY=-8 EndZ=0
    g5: LineSegment [constr] StartX=-15 StartY=-8 StartZ=0 EndX=-15 EndY=8 EndZ=0
    g6: ArcOfCircle CenterX=-15 CenterY=0 CenterZ=0 NormalX=0 NormalY=0 NormalZ=1 AngleXU=0 Radius=8 StartAngle=1.5708 EndAngle=4.71239
    g7: ArcOfCircle CenterX=15 CenterY=0 CenterZ=0 NormalX=0 NormalY=0 NormalZ=1 AngleXU=0 Radius=8 StartAngle=4.71239 EndAngle=7.85398
  constraints (22):
    c: PointOnObject(g0,g-1)
    c: PointOnObject(g1,g-1)
    c: Equal(g0,g1)
    c: Radius(g0) = 1.75
    c: Coincident(g2,g3)
    c: Coincident(g3,g4)
    c: Coincident(g4,g5)
    c: Coincident(g5,g2)
    c: Horizontal(g4)
    c: Vertical(g3)
    c: Vertical(g5)
    c: Symmetric(g2,g2,g-2)
    c: DistanceX(g2,g2) = 30
    c: PointOnObject(g0,g5)
    c: PointOnObject(g1,g3)
    c: DistanceY(g5,g5) = 16  'Width'
    c: Coincident(g6,g0)
    c: Coincident(g6,g2)
    c: Coincident(g6,g4)
    c: Coincident(g7,g1)
    c: Coincident(g7,g2)
    c: Coincident(g7,g3)
FEATURE [Sketcher::SketchObject] Sketch033  label="armadapter_hingebase001"
  MapMode = 5
  Placement = pos=(0,0,0) rot=(0.57735,0.57735,0.57735;2.0944rad)
  expr: Constraints.VerticalOffset = Constraints.Radius + Dimensions.BackJoinExtraLength
  expr: Constraints[15] = Screws.M3Radius
  sketch-geometry (6):
    g0: LineSegment StartX=-8 StartY=0 StartZ=0 EndX=8 EndY=0 EndZ=0
    g1: LineSegment StartX=8 StartY=0 StartZ=0 EndX=8 EndY=13 EndZ=0
    g2: LineSegment [constr] StartX=8 StartY=13 StartZ=0 EndX=-8 EndY=13 EndZ=0
    g3: LineSegment StartX=-8 StartY=13 StartZ=0 EndX=-8 EndY=0 EndZ=0
    g4: ArcOfCircle CenterX=0 CenterY=13 CenterZ=0 NormalX=0 NormalY=0 NormalZ=1 AngleXU=0 Radius=8 StartAngle=0 EndAngle=3.14159
    g5: Circle CenterX=0 CenterY=13 CenterZ=0 NormalX=0 NormalY=0 NormalZ=1 AngleXU=0 Radius=1.75
  constraints (17):
    c: Coincident(g0,g1)
    c: Coincident(g1,g2)
    c: Coincident(g2,g3)
    c: Coincident(g3,g0)
    c: Horizontal(g0)
    c: Horizontal(g2)
    c: Vertical(g1)
    c: Vertical(g3)
    c: PointOnObject(g0,g-1)
    c: Symmetric(g0,g0,g-2)
    c: PointOnObject(g4,g2)
    c: Coincident(g4,g2)
    c: Coincident(g4,g1)
    c: DistanceY(g3,g3) = 13  'VerticalOffset'
    c: Coincident(g5,g4)
    c: Radius(g5) = 1.75
    c: Radius(g4) = 8  'Radius'
FEATURE [Sketcher::SketchObject] Sketch034  label="armadapter_hingecavity001"
  MapMode = 5
  Placement = pos=(0,0,3) rot=(0.707107,0.707107,0;3.14159rad)
  expr: Placement.Base.z = armadapter_hingebase.Constraints.VerticalOffset - armadapter_hingebase.Constraints.Radius - 2mm
  expr: Constraints[10] = armadapter_backjoin.Constraints.Width
  sketch-geometry (4):
    g0: LineSegment StartX=-8 StartY=3.5 StartZ=0 EndX=8 EndY=3.5 EndZ=0
    g1: LineSegment StartX=8 StartY=3.5 StartZ=0 EndX=8 EndY=-3.5 EndZ=0
    g2: LineSegment StartX=8 StartY=-3.5 StartZ=0 EndX=-8 EndY=-3.5 EndZ=0
    g3: LineSegment StartX=-8 StartY=-3.5 StartZ=0 EndX=-8 EndY=3.5 EndZ=0
  constraints (12):
    c: Coincident(g0,g1)
    c: Coincident(g1,g2)
    c: Coincident(g2,g3)
    c: Coincident(g3,g0)
    c: Horizontal(g0)
    c: Horizontal(g2)
    c: Vertical(g1)
    c: Vertical(g3)
    c: Symmetric(g0,g2,g-1)
    c: DistanceY(g2,g0) = 7  'Width'
    c: DistanceX(g0,g0) = 16
    c: Symmetric(g0,g0,g-2)
FEATURE [Sketcher::SketchObject] Sketch035  label="sidearm_base"
  MapMode = 5
  sketch-geometry (10):
    g0: LineSegment StartX=-25.5 StartY=10 StartZ=0 EndX=25.5 EndY=10 EndZ=0
    g1: LineSegment StartX=27.5 StartY=8 StartZ=0 EndX=27.5 EndY=-8 EndZ=0
    g2: LineSegment StartX=25.5 StartY=-10 StartZ=0 EndX=-25.5 EndY=-10 EndZ=0
    g3: LineSegment StartX=-27.5 StartY=-8 StartZ=0 EndX=-27.5 EndY=8 EndZ=0
    g4: ArcOfCircle CenterX=25.5 CenterY=-8 CenterZ=0 NormalX=0 NormalY=0 NormalZ=1 AngleXU=0 Radius=2 StartAngle=4.71239 EndAngle=6.28319
    g5: ArcOfCircle CenterX=-25.5 CenterY=-8 CenterZ=0 NormalX=0 NormalY=0 NormalZ=1 AngleXU=0 Radius=2 StartAngle=3.14159 EndAngle=4.71239
    g6: ArcOfCircle CenterX=-25.5 CenterY=8 CenterZ=0 NormalX=0 NormalY=0 NormalZ=1 AngleXU=0 Radius=2 StartAngle=1.5708 EndAngle=3.14159
    g7: ArcOfCircle CenterX=25.5 CenterY=8 CenterZ=0 NormalX=0 NormalY=0 NormalZ=1 AngleXU=0 Radius=2 StartAngle=0 EndAngle=1.5708
    g8: Circle CenterX=-20 CenterY=0 CenterZ=0 NormalX=0 NormalY=0 NormalZ=1 AngleXU=0 Radius=2.2
    g9: Circle CenterX=20 CenterY=0 CenterZ=0 NormalX=0 NormalY=0 NormalZ=1 AngleXU=0 Radius=2.2
  constraints (25):
    c: Horizontal(g2)
    c: Vertical(g1)
    c: Vertical(g3)
    c: Tangent(g1,g4) = 1.5708
    c: Tangent(g2,g4) = 1.5708
    c: Tangent(g2,g5) = 1.5708
    c: Tangent(g3,g5) = 1.5708
    c: Tangent(g0,g6) = 1.5708
    c: Tangent(g3,g6) = 1.5708
    c: Tangent(g0,g7) = 1.5708
    c: Tangent(g1,g7) = 1.5708
    c: Radius(g6) = 2
    c: Equal(g7,g6)
    c: Equal(g6,g5)
    c: Equal(g5,g4)
    c: Symmetric(g2,g0,g-1)
    c: Symmetric(g0,g0,g-2)
    c: DistanceX(g3,g1) = 55
    c: DistanceY(g2,g0) = 20  'Width'
    c: PointOnObject(g8,g-1)
    c: PointOnObject(g9,g-1)
    c: Equal(g8,g9)
    c: Symmetric(g8,g9,g-2)
    c: DistanceX(g8,g9) = 40  'ScrewDistance'
    c: Radius(g8) = 2.2
FEATURE [Sketcher::SketchObject] Sketch036  label="sidearm_base_groove"
  MapMode = 5
  Placement = pos=(0,0,-2) rot=(1,0,0;3.14159rad)
  expr: Placement.Base.z = -SideArmBase.Length
  expr: Constraints[10] = arm_2020_base.Constraints.ScrewDistance - 12mm
  sketch-geometry (4):
    g0: LineSegment StartX=-14 StartY=3 StartZ=0 EndX=14 EndY=3 EndZ=0
    g1: LineSegment StartX=14 StartY=3 StartZ=0 EndX=14 EndY=-3 EndZ=0
    g2: LineSegment StartX=14 StartY=-3 StartZ=0 EndX=-14 EndY=-3 EndZ=0
    g3: LineSegment StartX=-14 StartY=-3 StartZ=0 EndX=-14 EndY=3 EndZ=0
  constraints (12):
    c: Coincident(g0,g1)
    c: Coincident(g1,g2)
    c: Coincident(g2,g3)
    c: Coincident(g3,g0)
    c: Horizontal(g0)
    c: Horizontal(g2)
    c: Vertical(g1)
    c: Vertical(g3)
    c: Symmetric(g0,g2,g-1)
    c: Symmetric(g0,g0,g-2)
    c: DistanceX(g0,g0) = 28
    c: DistanceY(g3,g3) = 6
FEATURE [Sketcher::SketchObject] Sketch037  label="sidearm_start_l"
  MapMode = 5
  expr: Constraints[5] = sidearm_base.Constraints.ScrewDistance - 13mm
  expr: Constraints.Width = sidearm_base.Constraints.Width
  sketch-geometry (4):
    g0: LineSegment StartX=-13.5 StartY=10 StartZ=0 EndX=13.5 EndY=10 EndZ=0
    g1: LineSegment StartX=13.5 StartY=10 StartZ=0 EndX=13.5 EndY=-10 EndZ=0
    g2: LineSegment StartX=13.5 StartY=-10 StartZ=0 EndX=-13.5 EndY=-10 EndZ=0
    g3: LineSegment StartX=-13.5 StartY=-10 StartZ=0 EndX=-13.5 EndY=10 EndZ=0
  constraints (13):
    c: Horizontal(g0)
    c: Horizontal(g2)
    c: Vertical(g1)
    c: Symmetric(g0,g2,g-1)
    c: Symmetric(g3,g1,g-2)
    c: DistanceX(g3,g1) = 27
    c: Coincident(g0,g1)
    c: Coincident(g0,g3)
    c: Coincident(g2,g3)
    c: Coincident(g1,g2)
    c: Equal(g0,g2)
    c: Equal(g3,g1)
    c: DistanceY(g3,g3) = 20  'Width'
FEATURE [Sketcher::SketchObject] Sketch038  label="sidearm_start_h"
  MapMode = 5
  Placement = pos=(0,0,35) rot=(0,0,1;0rad)
  expr: Constraints[11] = sidearm_base.Constraints.Width
  expr: Constraints.Width = armadapter_hingebase.Constraints.Radius * 2
  expr: Placement.Base.z = Dimensions.SideArmLength
  sketch-geometry (4):
    g0: LineSegment StartX=-8 StartY=10 StartZ=0 EndX=8 EndY=10 EndZ=0
    g1: LineSegment StartX=8 StartY=10 StartZ=0 EndX=8 EndY=-10 EndZ=0
    g2: LineSegment StartX=8 StartY=-10 StartZ=0 EndX=-8 EndY=-10 EndZ=0
    g3: LineSegment StartX=-8 StartY=-10 StartZ=0 EndX=-8 EndY=10 EndZ=0
  constraints (12):
    c: Coincident(g0,g1)
    c: Coincident(g1,g2)
    c: Coincident(g2,g3)
    c: Coincident(g3,g0)
    c: Horizontal(g0)
    c: Horizontal(g2)
    c: Vertical(g1)
    c: Vertical(g3)
    c: Symmetric(g0,g2,g-1)
    c: Symmetric(g0,g0,g-2)
    c: DistanceX(g0,g0) = 16  'Width'
    c: DistanceY(g3,g3) = 20
FEATURE [Sketcher::SketchObject] Sketch039  label="sidearm_hinge"
  MapMode = 5
  Placement = pos=(0,-10,35) rot=(0,0,1;3.14159rad)
  expr: Constraints.VerticalOffset = armadapter_hingebase.Constraints.VerticalOffset
  expr: Placement.Base.y = -sidearm_base.Constraints.Width / 2
  expr: Constraints.Radius = armadapter_hingebase.Constraints.Radius
  expr: Placement.Base.z = Dimensions.SideArmLength
  sketch-geometry (6):
    g0: LineSegment StartX=8 StartY=0 StartZ=0 EndX=-8 EndY=0 EndZ=0
    g1: LineSegment StartX=-8 StartY=0 StartZ=0 EndX=-8 EndY=13 EndZ=0
    g2: LineSegment StartX=8 StartY=13 StartZ=0 EndX=8 EndY=0 EndZ=0
    g3: ArcOfCircle CenterX=0 CenterY=13 CenterZ=0 NormalX=0 NormalY=0 NormalZ=1 AngleXU=0 Radius=8 StartAngle=0 EndAngle=3.14159
    g4: LineSegment [constr] StartX=-8 StartY=13 StartZ=0 EndX=8 EndY=13 EndZ=0
    g5: Circle CenterX=0 CenterY=13 CenterZ=0 NormalX=0 NormalY=0 NormalZ=1 AngleXU=0 Radius=1.75
  constraints (17):
    c: Coincident(g0,g1)
    c: Coincident(g2,g0)
    c: Vertical(g1)
    c: Vertical(g2)
    c: PointOnObject(g0,g-1)
    c: Symmetric(g0,g0,g-2)
    c: DistanceY(g1,g1) = 13  'VerticalOffset'
    c: PointOnObject(g3,g-2)
    c: Coincident(g3,g1)
    c: Coincident(g3,g2)
    c: Equal(g2,g1)
    c: Coincident(g4,g1)
    c: Coincident(g4,g2)
    c: PointOnObject(g3,g4)
    c: Coincident(g5,g3)
    c: Radius(g5) = 1.75
    c: Radius(g3) = 8  'Radius'
FEATURE [PartDesign::Pad] Pad019  label="SideArmBase"
  Length = 2
  Length2 = 100
  Profile = -> Sketch035
  Reversed = true
  Type = 0
FEATURE [PartDesign::Pad] Pad021  label="SideArmBaseGroove"
  BaseFeature = -> Pad019
  Length = 2.5
  Length2 = 100
  Profile = -> Sketch036
  Type = 0
FEATURE [PartDesign::AdditiveLoft] AdditiveLoft001
  BaseFeature = -> Pad021
  Closed = false
  Profile = -> Sketch037
  Ruled = false
  Sections = -> [Sketch038]
FEATURE [Sketcher::SketchObject] Sketch040  label="sidearm_start_m"
  MapMode = 5
  Placement = pos=(0,0,11.6667) rot=(0,0,1;0rad)
  expr: Constraints.Width = sidearm_base.Constraints.Width
  expr: Placement.Base.z = Dimensions.SideArmLength / 3
  sketch-geometry (4):
    g0: LineSegment StartX=-9 StartY=10 StartZ=0 EndX=9 EndY=10 EndZ=0
    g1: LineSegment StartX=9 StartY=10 StartZ=0 EndX=9 EndY=-10 EndZ=0
    g2: LineSegment StartX=9 StartY=-10 StartZ=0 EndX=-9 EndY=-10 EndZ=0
    g3: LineSegment StartX=-9 StartY=-10 StartZ=0 EndX=-9 EndY=10 EndZ=0
  constraints (13):
    c: Horizontal(g0)
    c: Horizontal(g2)
    c: Vertical(g1)
    c: Symmetric(g0,g2,g-1)
    c: Symmetric(g3,g1,g-2)
    c: DistanceX(g3,g1) = 18
    c: Coincident(g0,g1)
    c: Coincident(g0,g3)
    c: Coincident(g2,g3)
    c: Coincident(g1,g2)
    c: Equal(g0,g2)
    c: Equal(g3,g1)
    c: DistanceY(g3,g3) = 20  'Width'
FEATURE [Sketcher::SketchObject] Sketch041  label="sidearm_hingebase"
  MapMode = 5
  Placement = pos=(0,0,35) rot=(0,0,1;0rad)
  expr: Constraints[11] = sidearm_base.Constraints.Width
  expr: Constraints.Width = sidearm_start_h.Constraints.Width
  expr: Placement.Base.z = Dimensions.SideArmLength
  sketch-geometry (4):
    g0: LineSegment StartX=-8 StartY=10 StartZ=0 EndX=8 EndY=10 EndZ=0
    g1: LineSegment StartX=8 StartY=10 StartZ=0 EndX=8 EndY=-10 EndZ=0
    g2: LineSegment StartX=8 StartY=-10 StartZ=0 EndX=-8 EndY=-10 EndZ=0
    g3: LineSegment StartX=-8 StartY=-10 StartZ=0 EndX=-8 EndY=10 EndZ=0
  constraints (12):
    c: Coincident(g0,g1)
    c: Coincident(g1,g2)
    c: Coincident(g2,g3)
    c: Coincident(g3,g0)
    c: Horizontal(g0)
    c: Horizontal(g2)
    c: Vertical(g1)
    c: Vertical(g3)
    c: Symmetric(g0,g2,g-1)
    c: Symmetric(g0,g0,g-2)
    c: DistanceX(g0,g0) = 16  'Width'
    c: DistanceY(g3,g3) = 20
FEATURE [PartDesign::Fillet] Fillet006
  Base = -> AdditiveLoft001 [Edge12,Edge51]
  BaseFeature = -> AdditiveLoft001
  Radius = 2
FEATURE [PartDesign::Pad] Pad022  label="SideArmHingeBase"
  BaseFeature = -> Fillet006
  Length = 11.001
  Length2 = 100
  Profile = -> Sketch041
  Type = 0
  expr: Length = armadapter_hingecavity.Constraints.Width - 0.5mm + sidearm_hinge.Constraints.VerticalOffset - sidearm_hinge.Constraints.Radius - 0.5mm + 0.001mm
FEATURE [PartDesign::Pad] Pad023
  BaseFeature = -> Pad022
  Length = 6.5
  Length2 = 100
  Profile = -> Sketch039
  Refine = true
  Type = 0
  expr: Length = armadapter_hingecavity.Constraints.Width - 0.5mm
FEATURE [PartDesign::Fillet] Fillet004
  Base = -> Pad023 [Edge69]
  BaseFeature = -> Pad023
  Radius = 11
FEATURE [PartDesign::Fillet] Fillet005
  Base = -> Fillet004 [Edge26,Edge32]
  BaseFeature = -> Fillet004
  Radius = 4.5
  expr: Radius = sidearm_hinge.Constraints.VerticalOffset - sidearm_hinge.Constraints.Radius - 0.5mm
FEATURE [PartDesign::Fillet] Fillet007
  Base = -> Fillet005 [Edge12]
  BaseFeature = -> Fillet005
  Radius = 4.5
  expr: Radius = Fillet005.Radius
FEATURE [PartDesign::Body] Body006  label="SideArmBody"
  Group = -> [Sketch035,Sketch037,Sketch038,Sketch040,Sketch039,Sketch036,Pad019,Pad021,AdditiveLoft001,Fillet006,Pad022,Sketch041,Pad023,Fillet004,Fillet005,Fillet007]
  Origin = -> Origin010
  Tip = -> Fillet007
FEATURE [App::Part] Part006  label="SideArm"
  Group = -> [Body006]
  License = CC BY 3.0
  LicenseURL = http://creativecommons.org/licenses/by/3.0/
  Origin = -> Origin011
  Placement = pos=(-53.25,0,61) rot=(0.57735,0.57735,0.57735;2.0944rad)
FEATURE [PartDesign::Fillet] Fillet008
  Base = -> Fillet001 [Edge34,Edge21]
  BaseFeature = -> Fillet001
  Placement = pos=(0,0,0) rot=(0.57735,0.57735,0.57735;2.0944rad)
  Radius = 2
FEATURE [PartDesign::Body] Body002  label="AdapterBody"
  Group = -> [Sketch011,Sketch012,Sketch010,Pad008,Pad009,Pocket002,Fillet001,Fillet008]
  Origin = -> Origin003
  Tip = -> Fillet008
FEATURE [App::Part] Part004  label="Adapter"
  Group = -> [Body002]
  License = CC BY 3.0
  LicenseURL = http://creativecommons.org/licenses/by/3.0/
  Origin = -> Origin009
FEATURE [Sketcher::SketchObject] Sketch042  label="back_enforcement"
  AttachmentOffset = pos=(0,0,1.8) rot=(0,0,1;0rad)
  MapMode = 5
  Placement = pos=(0,0,1.8) rot=(0,0,1;0rad)
  Support = -> [XY_Plane001]
  expr: Constraints[12] = Sketch007.Constraints.AttacherHoleDistance
  expr: AttachmentOffset.Base.z = BackPanel.Length
  expr: Constraints.Inner = Screws.M3NutRadius
  expr: Constraints[43] = Constraints.Inner + 1.23mm
  sketch-geometry (29):
    g0: Circle CenterX=-15 CenterY=-15 CenterZ=0 NormalX=0 NormalY=0 NormalZ=1 AngleXU=0 Radius=3.4
    g1: Circle CenterX=15 CenterY=-15 CenterZ=0 NormalX=0 NormalY=0 NormalZ=1 AngleXU=0 Radius=3.4
    g2: Circle CenterX=15 CenterY=15 CenterZ=0 NormalX=0 NormalY=0 NormalZ=1 AngleXU=0 Radius=3.4
    g3: Circle CenterX=-15 CenterY=15 CenterZ=0 NormalX=0 NormalY=0 NormalZ=1 AngleXU=0 Radius=3.4
    g4: LineSegment [constr] StartX=-15 StartY=15 StartZ=0 EndX=15 EndY=15 EndZ=0
    g5: LineSegment [constr] StartX=15 StartY=15 StartZ=0 EndX=15 EndY=-15 EndZ=0
    g6: LineSegment [constr] StartX=15 StartY=-15 StartZ=0 EndX=-15 EndY=-15 EndZ=0
    g7: LineSegment [constr] StartX=-15 StartY=-15 StartZ=0 EndX=-15 EndY=15 EndZ=0
    g8: LineSegment StartX=-15.615 StartY=10.411 StartZ=0 EndX=-15.615 EndY=-10.411 EndZ=0
    g9: LineSegment StartX=-14.385 StartY=10.411 StartZ=0 EndX=-14.385 EndY=-10.411 EndZ=0
    g10: LineSegment [constr] StartX=-15.615 StartY=10.411 StartZ=0 EndX=-14.385 EndY=10.411 EndZ=0
    g11: LineSegment StartX=-10.411 StartY=15.615 StartZ=0 EndX=10.411 EndY=15.615 EndZ=0
    g12: LineSegment StartX=10.411 StartY=14.385 StartZ=0 EndX=-10.411 EndY=14.385 EndZ=0
    g13: ArcOfCircle CenterX=-15 CenterY=15 CenterZ=0 NormalX=0 NormalY=0 NormalZ=1 AngleXU=0 Radius=4.63 StartAngle=0.133223 EndAngle=4.57917
    g14: ArcOfCircle CenterX=-15 CenterY=15 CenterZ=0 NormalX=0 NormalY=0 NormalZ=1 AngleXU=0 Radius=4.63 StartAngle=4.84561 EndAngle=6.14996
    g15: LineSegment [constr] StartX=14.385 StartY=10.411 StartZ=0 EndX=15.615 EndY=10.411 EndZ=0
    g16: LineSegment StartX=15.615 StartY=10.411 StartZ=0 EndX=15.615 EndY=-10.411 EndZ=0
    g17: LineSegment [constr] StartX=15.615 StartY=-10.411 StartZ=0 EndX=14.385 EndY=-10.411 EndZ=0
    g18: LineSegment StartX=14.385 StartY=-10.411 StartZ=0 EndX=14.385 EndY=10.411 EndZ=0
    g19: LineSegment StartX=-10.411 StartY=-14.385 StartZ=0 EndX=10.411 EndY=-14.385 EndZ=0
    g20: LineSegment StartX=10.411 StartY=-15.615 StartZ=0 EndX=-10.411 EndY=-15.615 EndZ=0
    g21: LineSegment [constr] StartX=-10.411 StartY=-15.615 StartZ=0 EndX=-10.411 EndY=-14.385 EndZ=0
    g22: ArcOfCircle CenterX=15 CenterY=-15 CenterZ=0 NormalX=0 NormalY=0 NormalZ=1 AngleXU=0 Radius=4.63 StartAngle=3.27482 EndAngle=7.72076
    g23: ArcOfCircle CenterX=15 CenterY=-15 CenterZ=0 NormalX=0 NormalY=0 NormalZ=1 AngleXU=0 Radius=4.63 StartAngle=1.70402 EndAngle=3.00837
    g24: ArcOfCircle CenterX=-15 CenterY=-15 CenterZ=0 NormalX=0 NormalY=0 NormalZ=1 AngleXU=0 Radius=4.63 StartAngle=1.70402 EndAngle=6.14996
    g25: ArcOfCircle CenterX=-15 CenterY=-15 CenterZ=0 NormalX=0 NormalY=0 NormalZ=1 AngleXU=0 Radius=4.63 StartAngle=0.133223 EndAngle=1.43757
    g26: ArcOfCircle CenterX=15 CenterY=15 CenterZ=0 NormalX=0 NormalY=0 NormalZ=1 AngleXU=0 Radius=4.63 StartAngle=4.84561 EndAngle=9.29155
    g27: ArcOfCircle CenterX=15 CenterY=15 CenterZ=0 NormalX=0 NormalY=0 NormalZ=1 AngleXU=0 Radius=4.63 StartAngle=3.27482 EndAngle=4.57917
    g28: LineSegment [constr] StartX=10.411 StartY=15.615 StartZ=0 EndX=10.411 EndY=14.385 EndZ=0
  constraints (76):
    c: Equal(g1,g2)
    c: Equal(g2,g3)
    c: Equal(g3,g0)
    c: Coincident(g4,g5)
    c: Coincident(g5,g6)
    c: Coincident(g6,g7)
    c: Coincident(g7,g4)
    c: Horizontal(g4)
    c: Horizontal(g6)
    c: Vertical(g5)
    c: Vertical(g7)
    c: Equal(g6,g5)
    c: DistanceX(g6,g6) = 30
    c: Radius(g1) = 3.4  'Inner'
    c: Vertical(g8)
    c: Vertical(g9)
    c: Symmetric(g8,g9,g7)
    c: Coincident(g10,g8)
    c: Coincident(g10,g9)
    c: DistanceX(g10,g10) = 1.23
    c: Horizontal(g11)
    c: Horizontal(g12)
    c: Coincident(g13,g3)
    c: Coincident(g13,g11)
    c: Coincident(g13,g8)
    c: Coincident(g14,g3)
    c: Coincident(g14,g9)
    c: Coincident(g12,g14)
    c: Coincident(g15,g16)
    c: Coincident(g16,g17)
    c: Coincident(g17,g18)
    c: Coincident(g18,g15)
    c: Horizontal(g15)
    c: Horizontal(g17)
    c: Vertical(g16)
    c: Vertical(g18)
    c: Coincident(g20,g21)
    c: Coincident(g21,g19)
    c: Horizontal(g19)
    c: Horizontal(g20)
    c: Vertical(g21)
    c: Coincident(g22,g1)
    c: Coincident(g22,g16)
    c: Radius(g22) = 4.63
    c: Coincident(g1,g5)
    c: Coincident(g23,g1)
    c: Coincident(g23,g17)
    c: Coincident(g23,g19)
    c: Coincident(g0,g6)
    c: Coincident(g24,g0)
    c: Coincident(g24,g8)
    c: Coincident(g24,g20)
    c: Coincident(g25,g0)
    c: Coincident(g25,g9)
    c: Coincident(g25,g19)
    c: Coincident(g26,g4)
    c: Coincident(g26,g15)
    c: Coincident(g26,g11)
    c: Coincident(g27,g12)
    c: Coincident(g27,g15)
    c: Coincident(g2,g4)
    c: Coincident(g2,g27)
    c: Coincident(g3,g4)
    c: Equal(g22,g23)
    c: Equal(g23,g26)
    c: Equal(g27,g13)
    c: Equal(g14,g24)
    c: Equal(g24,g25)
    c: Coincident(g20,g22)
    c: Coincident(g28,g11)
    c: Coincident(g28,g12)
    c: Vertical(g28)
    c: Equal(g10,g21)
    c: Equal(g21,g17)
    c: Equal(g17,g28)
    c: Symmetric(g0,g2,g-1)
FEATURE [Sketcher::SketchObject] Sketch043  label="backinnerwalls"
  MapMode = 5
  Placement = pos=(0,0,5.8) rot=(0,0,1;0rad)
  expr: Constraints[67] = Dimensions.InnerWallThickness
  expr: Constraints[7] = Dimensions.PCBHeight + 2 * Dimensions.PCBGap - 2 * Dimensions.InnerWallGap
  expr: Placement.Base.z = backwalls.Placement.Base.z + BackWalls.Length
  expr: Constraints[6] = Dimensions.PCBWidth + 2 * Dimensions.PCBGap - 2 * Dimensions.InnerWallGap
  sketch-geometry (24):
    g0: LineSegment StartX=47.35 StartY=44.35 StartZ=0 EndX=47.35 EndY=-44.35 EndZ=0
    g1: LineSegment StartX=-1 StartY=-44.35 StartZ=0 EndX=-47.35 EndY=-44.35 EndZ=0
    g2: LineSegment StartX=-47.35 StartY=-44.35 StartZ=0 EndX=-47.35 EndY=44.35 EndZ=0
    g3: LineSegment StartX=46.15 StartY=43.15 StartZ=0 EndX=46.15 EndY=-43.15 EndZ=0
    g4: LineSegment StartX=-1 StartY=-43.15 StartZ=0 EndX=-46.15 EndY=-43.15 EndZ=0
    g5: LineSegment StartX=-46.15 StartY=-43.15 StartZ=0 EndX=-46.15 EndY=43.15 EndZ=0
    g6: LineSegment StartX=-46.15 StartY=43.15 StartZ=0 EndX=-1 EndY=43.15 EndZ=0
    g7: LineSegment StartX=-1 StartY=43.15 StartZ=0 EndX=-1 EndY=44.35 EndZ=0
    g8: LineSegment StartX=-1 StartY=44.35 StartZ=0 EndX=-47.35 EndY=44.35 EndZ=0
    g9: LineSegment StartX=46.15 StartY=43.15 StartZ=0 EndX=1 EndY=43.15 EndZ=0
    g10: LineSegment StartX=1 StartY=43.15 StartZ=0 EndX=1 EndY=44.35 EndZ=0
    g11: LineSegment StartX=1 StartY=44.35 StartZ=0 EndX=47.35 EndY=44.35 EndZ=0
    g12: LineSegment [constr] StartX=-1 StartY=44.35 StartZ=0 EndX=1 EndY=44.35 EndZ=0
    g13: LineSegment StartX=46.15 StartY=-43.15 StartZ=0 EndX=1 EndY=-43.15 EndZ=0
    g14: LineSegment StartX=1 StartY=-43.15 StartZ=0 EndX=1 EndY=-44.35 EndZ=0
    g15: LineSegment StartX=1 StartY=-44.35 StartZ=0 EndX=47.35 EndY=-44.35 EndZ=0
    g16: LineSegment StartX=-1 StartY=-43.15 StartZ=0 EndX=-1 EndY=-44.35 EndZ=0
    g17: LineSegment [constr] StartX=-1 StartY=-43.15 StartZ=0 EndX=1 EndY=-43.15 EndZ=0
    g18: LineSegment [constr] StartX=-1 StartY=-44.35 StartZ=0 EndX=1 EndY=-44.35 EndZ=0
    g19: LineSegment [constr] StartX=-1 StartY=43.15 StartZ=0 EndX=1 EndY=43.15 EndZ=0
    g20: LineSegment [constr] StartX=-46.15 StartY=-43.15 StartZ=0 EndX=-47.35 EndY=-43.15 EndZ=0
    g21: LineSegment [constr] StartX=-46.15 StartY=43.15 StartZ=0 EndX=-46.15 EndY=44.35 EndZ=0
    g22: LineSegment [constr] StartX=46.15 StartY=43.15 StartZ=0 EndX=47.35 EndY=43.15 EndZ=0
    g23: LineSegment [constr] StartX=46.15 StartY=-43.15 StartZ=0 EndX=46.15 EndY=-44.35 EndZ=0
  constraints (68):
    c: Coincident(g1,g2)
    c: Horizontal(g1)
    c: Vertical(g0)
    c: Vertical(g2)
    c: Symmetric(g2,g0,g-2)
    c: Symmetric(g2,g1,g-1)
    c: DistanceX(g2,g0) = 94.7
    c: DistanceY(g2,g2) = 88.7
    c: Coincident(g4,g5)
    c: Horizontal(g4)
    c: Vertical(g3)
    c: Vertical(g5)
    c: Symmetric(g5,g3,g-2)
    c: Symmetric(g5,g4,g-1)
    c: Coincident(g5,g6)
    c: Horizontal(g6)
    c: Coincident(g6,g7)
    c: Vertical(g7)
    c: Coincident(g7,g8)
    c: Coincident(g8,g2)
    c: Horizontal(g8)
    c: Coincident(g3,g9)
    c: Horizontal(g9)
    c: Coincident(g9,g10)
    c: Vertical(g10)
    c: Coincident(g10,g11)
    c: Coincident(g11,g0)
    c: Horizontal(g11)
    c: Coincident(g12,g7)
    c: Coincident(g12,g10)
    c: Symmetric(g7,g10,g-2)
    c: DistanceX(g12,g12) = 2
    c: Coincident(g3,g13)
    c: Horizontal(g13)
    c: Coincident(g13,g14)
    c: Vertical(g14)
    c: Coincident(g14,g15)
    c: Coincident(g15,g0)
    c: Horizontal(g15)
    c: Coincident(g16,g4)
    c: Coincident(g16,g1)
    c: Vertical(g16)
    c: Coincident(g17,g4)
    c: Coincident(g17,g13)
    c: Coincident(g18,g1)
    c: Coincident(g18,g14)
    c: Horizontal(g18)
    c: Symmetric(g4,g13,g-2)
    c: Equal(g18,g17)
    c: Equal(g17,g12)
    c: Coincident(g19,g6)
    c: Coincident(g19,g9)
    c: Coincident(g20,g4)
    c: PointOnObject(g20,g2)
    c: Horizontal(g20)
    c: Coincident(g21,g5)
    c: PointOnObject(g21,g8)
    c: Vertical(g21)
    c: Coincident(g22,g3)
    c: PointOnObject(g22,g0)
    c: Horizontal(g22)
    c: Coincident(g23,g3)
    c: PointOnObject(g23,g15)
    c: Vertical(g23)
    c: Equal(g20,g21)
    c: Equal(g21,g22)
    c: Equal(g22,g23)
    c: DistanceX(g20,g20) = 1.2
FEATURE [PartDesign::Pad] Pad025  label="BackInnerWalls"
  BaseFeature = -> Pad004
  Length = 2
  Length2 = 100
  Profile = -> Sketch043
  Refine = true
  Type = 0
FEATURE [PartDesign::Fillet] Fillet002
  Base = -> Pad025 [Edge30,Edge27,Edge29,Edge28,Edge97,Edge21,Edge26,Edge98]
  BaseFeature = -> Pad025
  Radius = 1.799
  expr: Radius = Spreadsheet.PanelThickness - 0.001mm
FEATURE [PartDesign::Pad] Pad006  label="BackNuts2"
  BaseFeature = -> Fillet002
  Length = 4
  Length2 = 100
  Profile = -> Sketch009
  Type = 0
  expr: Length = BackWalls.Length
FEATURE [PartDesign::Pad] Pad007  label="BackNuts3"
  BaseFeature = -> Pad006
  Length = 3.2
  Length2 = 100
  Profile = -> Sketch006
  Refine = true
  Type = 0
FEATURE [Sketcher::SketchObject] Sketch044  label="backnuts"
  MapMode = 5
  expr: Constraints[102] = Dimensions.HoleDistanceH
  expr: Constraints[9] = Dimensions.PCBWidth
  expr: Constraints[109] = Dimensions.HoleDistanceV
  expr: Constraints[101] = Screws.M3NutRadius
  expr: Constraints[110] = Dimensions.PCBHeight / 2 - Dimensions.HoleDistanceTop
  expr: Constraints[10] = Dimensions.PCBHeight
  expr: Constraints[19] = Dimensions.LCDHeight
  expr: Constraints[20] = Dimensions.LCDWidth
  sketch-geometry (38):
    g0: LineSegment [constr] StartX=-44 StartY=41.5 StartZ=0 EndX=44 EndY=41.5 EndZ=0
    g1: LineSegment [constr] StartX=-44 StartY=-24 StartZ=0 EndX=44 EndY=-24 EndZ=0
    g2: LineSegment [constr] StartX=-46.5 StartY=43.5 StartZ=0 EndX=46.5 EndY=43.5 EndZ=0
    g3: LineSegment [constr] StartX=46.5 StartY=43.5 StartZ=0 EndX=46.5 EndY=-43.5 EndZ=0
    g4: LineSegment [constr] StartX=46.5 StartY=-43.5 StartZ=0 EndX=-46.5 EndY=-43.5 EndZ=0
    g5: LineSegment [constr] StartX=-46.5 StartY=-43.5 StartZ=0 EndX=-46.5 EndY=43.5 EndZ=0
    g6: LineSegment [constr] StartX=-39 StartY=34.5 StartZ=0 EndX=39 EndY=34.5 EndZ=0
    g7: LineSegment [constr] StartX=39 StartY=34.5 StartZ=0 EndX=39 EndY=-16.5 EndZ=0
    g8: LineSegment [constr] StartX=39 StartY=-16.5 StartZ=0 EndX=-39 EndY=-16.5 EndZ=0
    g9: LineSegment [constr] StartX=-39 StartY=-16.5 StartZ=0 EndX=-39 EndY=34.5 EndZ=0
    g10: LineSegment StartX=-42.3 StartY=38.5555 StartZ=0 EndX=-40.6 EndY=41.5 EndZ=0
    g11: LineSegment StartX=-40.6 StartY=41.5 StartZ=0 EndX=-42.3 EndY=44.4445 EndZ=0
    g12: LineSegment StartX=-42.3 StartY=44.4445 StartZ=0 EndX=-45.7 EndY=44.4445 EndZ=0
    g13: LineSegment StartX=-45.7 StartY=44.4445 StartZ=0 EndX=-47.4 EndY=41.5 EndZ=0
    g14: LineSegment StartX=-47.4 StartY=41.5 StartZ=0 EndX=-45.7 EndY=38.5555 EndZ=0
    g15: LineSegment StartX=-45.7 StartY=38.5555 StartZ=0 EndX=-42.3 EndY=38.5555 EndZ=0
    g16: Circle [constr] CenterX=-44 CenterY=41.5 CenterZ=0 NormalX=0 NormalY=0 NormalZ=1 AngleXU=0 Radius=3.4
    g17: LineSegment StartX=45.7 StartY=38.5555 StartZ=0 EndX=47.4 EndY=41.5 EndZ=0
    g18: LineSegment StartX=47.4 StartY=41.5 StartZ=0 EndX=45.7 EndY=44.4445 EndZ=0
    g19: LineSegment StartX=45.7 StartY=44.4445 StartZ=0 EndX=42.3 EndY=44.4445 EndZ=0
    g20: LineSegment StartX=42.3 StartY=44.4445 StartZ=0 EndX=40.6 EndY=41.5 EndZ=0
    g21: LineSegment StartX=40.6 StartY=41.5 StartZ=0 EndX=42.3 EndY=38.5555 EndZ=0
    g22: LineSegment StartX=42.3 StartY=38.5555 StartZ=0 EndX=45.7 EndY=38.5555 EndZ=0
    g23: Circle [constr] CenterX=44 CenterY=41.5 CenterZ=0 NormalX=0 NormalY=0 NormalZ=1 AngleXU=0 Radius=3.4
    g24: LineSegment StartX=45.7 StartY=-26.9445 StartZ=0 EndX=47.4 EndY=-24 EndZ=0
    g25: LineSegment StartX=47.4 StartY=-24 StartZ=0 EndX=45.7 EndY=-21.0555 EndZ=0
    g26: LineSegment StartX=45.7 StartY=-21.0555 StartZ=0 EndX=42.3 EndY=-21.0555 EndZ=0
    g27: LineSegment StartX=42.3 StartY=-21.0555 StartZ=0 EndX=40.6 EndY=-24 EndZ=0
    g28: LineSegment StartX=40.6 StartY=-24 StartZ=0 EndX=42.3 EndY=-26.9445 EndZ=0
    g29: LineSegment StartX=42.3 StartY=-26.9445 StartZ=0 EndX=45.7 EndY=-26.9445 EndZ=0
    g30: Circle [constr] CenterX=44 CenterY=-24 CenterZ=0 NormalX=0 NormalY=0 NormalZ=1 AngleXU=0 Radius=3.4
    g31: LineSegment StartX=-42.3 StartY=-26.9445 StartZ=0 EndX=-40.6 EndY=-24 EndZ=0
    g32: LineSegment StartX=-40.6 StartY=-24 StartZ=0 EndX=-42.3 EndY=-21.0555 EndZ=0
    g33: LineSegment StartX=-42.3 StartY=-21.0555 StartZ=0 EndX=-45.7 EndY=-21.0555 EndZ=0
    g34: LineSegment StartX=-45.7 StartY=-21.0555 StartZ=0 EndX=-47.4 EndY=-24 EndZ=0
    g35: LineSegment StartX=-47.4 StartY=-24 StartZ=0 EndX=-45.7 EndY=-26.9445 EndZ=0
    g36: LineSegment StartX=-45.7 StartY=-26.9445 StartZ=0 EndX=-42.3 EndY=-26.9445 EndZ=0
    g37: Circle [constr] CenterX=-44 CenterY=-24 CenterZ=0 NormalX=0 NormalY=0 NormalZ=1 AngleXU=0 Radius=3.4
  constraints (95):
    c: Equal(g0,g1)
    c: Coincident(g2,g3)
    c: Coincident(g3,g4)
    c: Coincident(g4,g5)
    c: Coincident(g5,g2)
    c: Horizontal(g2)
    c: Horizontal(g4)
    c: Vertical(g3)
    c: Vertical(g5)
    c: DistanceX(g2,g2) = 93
    c: DistanceY(g5,g5) = 87
    c: Coincident(g6,g7)
    c: Coincident(g7,g8)
    c: Coincident(g8,g9)
    c: Coincident(g9,g6)
    c: Horizontal(g6)
    c: Horizontal(g8)
    c: Vertical(g7)
    c: Vertical(g9)
    c: DistanceY(g9,g9) = 51
    c: DistanceX(g6,g6) = 78
    c: DistanceY(g6,g2) = 9
    c: Symmetric(g4,g3,g-2)
    c: Symmetric(g2,g2,g-2)
    c: Symmetric(g2,g4,g-1)
    c: Symmetric(g6,g6,g-2)
    c: Coincident(g10,g11)
    c: Coincident(g11,g12)
    c: Coincident(g12,g13)
    c: Coincident(g13,g14)
    c: Coincident(g14,g15)
    c: Coincident(g15,g10)
    c: Equal(g10, g11-g15) x5
    c: PointOnObject(g10,g16)
    c: PointOnObject(g11,g16)
    c: PointOnObject(g12,g16)
    c: PointOnObject(g13,g16)
    c: PointOnObject(g14,g16)
    c: PointOnObject(g15,g16)
    c: Coincident(g17,g18)
    c: Coincident(g18,g19)
    c: Coincident(g19,g20)
    c: Coincident(g20,g21)
    c: Coincident(g21,g22)
    c: Coincident(g22,g17)
    c: Equal(g17, g18-g22) x5
    c: PointOnObject(g17,g23)
    c: PointOnObject(g18,g23)
    c: PointOnObject(g19,g23)
    c: PointOnObject(g20,g23)
    c: PointOnObject(g21,g23)
    c: PointOnObject(g22,g23)
    c: Coincident(g24,g25)
    c: Coincident(g25,g26)
    c: Coincident(g26,g27)
    c: Coincident(g27,g28)
    c: Coincident(g28,g29)
    c: Coincident(g29,g24)
    c: Equal(g24, g25-g29) x5
    c: PointOnObject(g24,g30)
    c: PointOnObject(g25,g30)
    c: PointOnObject(g26,g30)
    c: PointOnObject(g27,g30)
    c: PointOnObject(g28,g30)
    c: PointOnObject(g29,g30)
    c: Coincident(g31,g32)
    c: Coincident(g32,g33)
    c: Coincident(g33,g34)
    c: Coincident(g34,g35)
    c: Coincident(g35,g36)
    c: Coincident(g36,g31)
    c: Equal(g31, g32-g36) x5
    c: PointOnObject(g31,g37)
    c: PointOnObject(g32,g37)
    c: PointOnObject(g33,g37)
    c: PointOnObject(g34,g37)
    c: PointOnObject(g35,g37)
    c: PointOnObject(g36,g37)
    c: Horizontal(g12)
    c: Horizontal(g19)
    c: Horizontal(g26)
    c: Horizontal(g33)
    c: Equal(g37,g30)
    c: Equal(g30,g23)
    c: Equal(g23,g16)
    c: Radius(g30) = 3.4
    c: DistanceX(g0,g0) = 88
    c: Symmetric(g0,g0,g-2)
    c: Coincident(g23,g0)
    c: Coincident(g16,g0)
    c: Symmetric(g1,g1,g-2)
    c: Coincident(g37,g1)
    c: Coincident(g1,g30)
    c: DistanceY(g1,g0) = 65.5
    c: DistanceY(g-1,g0) = 41.5
FEATURE [PartDesign::Pocket] Pocket005  label="BackNuts"
  BaseFeature = -> Pad007
  Length = 2.6
  Length2 = 100
  Profile = -> Sketch044
  Reversed = true
  Type = 0
  expr: Length = Screws.M3NutHeight
FEATURE [PartDesign::Pad] Pad024  label="BackEnforcement"
  BaseFeature = -> Pocket005
  Length = 3.5
  Length2 = 100
  Profile = -> Sketch042
  Type = 0
  expr: Length = Screws.M3HeadHeight + 0.10000000000000001mm
FEATURE [PartDesign::Fillet] Fillet009
  Base = -> Pad024 [Face134,Edge239,Edge238,Edge237,Edge236,Edge235,Edge234,Edge241,Edge240]
  BaseFeature = -> Pad024
  Radius = 3.499
  expr: Radius = BackEnforcement.Length - 0.001mm
FEATURE [PartDesign::Body] Body001  label="BackBody"
  Group = -> [Sketch007,Sketch005,Sketch009,Sketch006,Pad003,Pad004,Pad025,Fillet002,Pad006,Pad007,Pocket005,Pad024,Sketch042,Sketch043,Sketch044,Fillet009]
  Origin = -> Origin001
  Tip = -> Fillet009
FEATURE [App::Part] Part001  label="Back"
  Group = -> [Body001]
  License = CC BY 3.0
  LicenseURL = http://creativecommons.org/licenses/by/3.0/
  Origin = -> Origin005
  Placement = pos=(0,0,23.3) rot=(0,1,0;3.14159rad)
